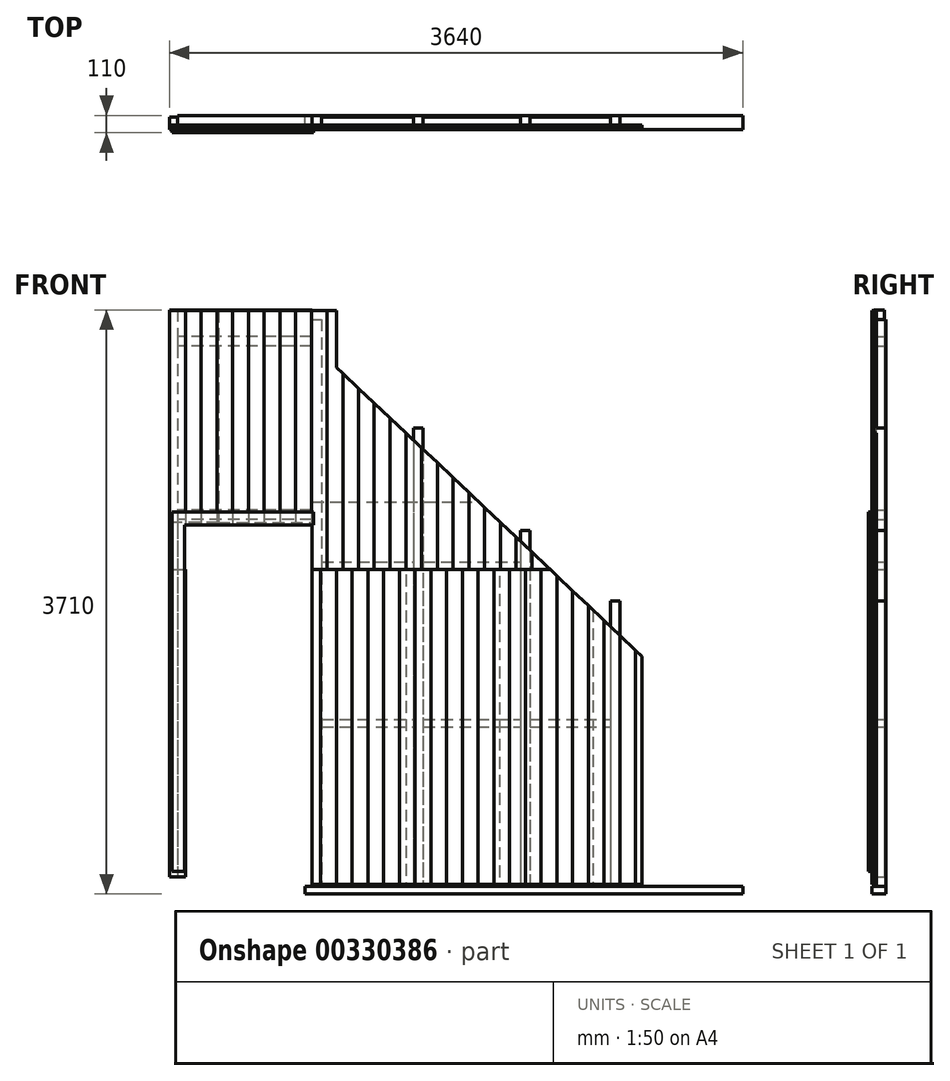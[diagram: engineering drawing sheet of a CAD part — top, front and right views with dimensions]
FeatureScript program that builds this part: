
annotation { "Feature Type Name" : "Feature", "Feature Type Description" : "" }
export const myFeature = defineFeature(function(context is Context, id is Id, definition is map)
    precondition{}
    {
        {
            var Q0;
            Q0=qCreatedBy(makeId("Top.planeOp"),FACE);
            var sketch = newSketch(context, id + "F0", { "sketchPlane" : qUnion([Q0])});
            skLineSegment(sketch, "E0.bottom", {"start": v(0, 0) * mm, "end": v(2780, 0) * mm});
            skLineSegment(sketch, "E0.top", {"start": v(0, 90) * mm, "end": v(2780, 90) * mm});
            skLineSegment(sketch, "E0.left", {"start": v(0, 0) * mm, "end": v(0, 90) * mm});
            skLineSegment(sketch, "E0.right", {"start": v(2780, 0) * mm, "end": v(2780, 90) * mm});
            skSolve(sketch);
        }
        {
            var Q0;
            Q0=makeQuery(id+"F0.imprint","IMPRINT",FACE,{"disambiguationData":[TD([[makeQuery(id+"F0.imprint","IMPRINT",EDGE,{"derivedFrom":sQuery(id+"F0.wireOp",EDGE,"E0.bottom")}),1.0]])]});
            extrude(context, id + "F1", {"entities" : qUnion([Q0]), "depth" : 50 * mm});
        }
        {
            var Q0;
            Q0=qCreatedBy(makeId("Top.planeOp"),FACE);
            var sketch = newSketch(context, id + "F2", { "sketchPlane" : qUnion([Q0])});
            skLineSegment(sketch, "E1", {"start": v(0, 0) * mm, "end": v(10, 0) * mm});
            skLineSegment(sketch, "E2", {"start": v(0, 0) * mm, "end": v(-810, 0) * mm});
            skLineSegment(sketch, "E3.bottom", {"start": v(10, 0) * mm, "end": v(70, 0) * mm});
            skLineSegment(sketch, "E3.top", {"start": v(10, 60) * mm, "end": v(70, 60) * mm});
            skLineSegment(sketch, "E3.left", {"start": v(10, 0) * mm, "end": v(10, 60) * mm});
            skLineSegment(sketch, "E3.right", {"start": v(70, 0) * mm, "end": v(70, 60) * mm});
            skLineSegment(sketch, "E4.bottom", {"start": v(-810, 0) * mm, "end": v(-860, 0) * mm});
            skLineSegment(sketch, "E4.top", {"start": v(-810, 50) * mm, "end": v(-860, 50) * mm});
            skLineSegment(sketch, "E4.left", {"start": v(-810, 0) * mm, "end": v(-810, 50) * mm});
            skLineSegment(sketch, "E4.right", {"start": v(-860, 0) * mm, "end": v(-860, 50) * mm});
            skLineSegment(sketch, "E5", {"start": v(0, 0) * mm, "end": v(2020, 0) * mm});
            skLineSegment(sketch, "E6", {"start": v(70, 60) * mm, "end": v(690, 60) * mm});
            skLineSegment(sketch, "E7.bottom", {"start": v(690, 60) * mm, "end": v(750, 60) * mm});
            skLineSegment(sketch, "E7.top", {"start": v(690, 0) * mm, "end": v(750, 0) * mm});
            skLineSegment(sketch, "E7.left", {"start": v(690, 60) * mm, "end": v(690, 0) * mm});
            skLineSegment(sketch, "E7.right", {"start": v(750, 60) * mm, "end": v(750, 0) * mm});
            skLineSegment(sketch, "E8", {"start": v(750, 60) * mm, "end": v(1370, 60) * mm});
            skLineSegment(sketch, "E9.bottom", {"start": v(1370, 60) * mm, "end": v(1430, 60) * mm});
            skLineSegment(sketch, "E9.top", {"start": v(1370, 0) * mm, "end": v(1430, 0) * mm});
            skLineSegment(sketch, "E9.left", {"start": v(1370, 60) * mm, "end": v(1370, 0) * mm});
            skLineSegment(sketch, "E9.right", {"start": v(1430, 60) * mm, "end": v(1430, 0) * mm});
            skLineSegment(sketch, "E10", {"start": v(1430, 60) * mm, "end": v(1940, 60) * mm});
            skLineSegment(sketch, "E11.bottom", {"start": v(1940, 60) * mm, "end": v(2000, 60) * mm});
            skLineSegment(sketch, "E11.top", {"start": v(1940, 0) * mm, "end": v(2000, 0) * mm});
            skLineSegment(sketch, "E11.left", {"start": v(1940, 60) * mm, "end": v(1940, 0) * mm});
            skLineSegment(sketch, "E11.right", {"start": v(2000, 60) * mm, "end": v(2000, 0) * mm});
            skSolve(sketch);
        }
        {
            var Q0;
            Q0=makeQuery(id+"F2.imprint","IMPRINT",FACE,{"disambiguationData":[TD([[makeQuery(id+"F2.imprint","IMPRINT",EDGE,{"derivedFrom":sQuery(id+"F2.wireOp",EDGE,"E4.bottom")}),-1.0]])]});
            var Q1;
            Q1=makeQuery(id+"F2.imprint","IMPRINT",FACE,{"disambiguationData":[TD([[makeQuery(id+"F2.imprint","IMPRINT",EDGE,{"derivedFrom":sQuery(id+"F2.wireOp",EDGE,"E3.top")}),-1.0]])]});
            extrude(context, id + "F3", {"entities" : qUnion([Q0, Q1]), "depth" : 3600 * mm});
        }
        {
            var Q0;
            Q0=makeQuery(id+"F2.imprint","IMPRINT",FACE,{"disambiguationData":[TD([[makeQuery(id+"F2.imprint","IMPRINT",EDGE,{"derivedFrom":sQuery(id+"F2.wireOp",EDGE,"E7.bottom")}),-1.0]])]});
            extrude(context, id + "F4", {"entities" : qUnion([Q0]), "depth" : 2910 * mm});
        }
        {
            var Q0;
            Q0=makeQuery(id+"F2.imprint","IMPRINT",FACE,{"disambiguationData":[TD([[makeQuery(id+"F2.imprint","IMPRINT",EDGE,{"derivedFrom":sQuery(id+"F2.wireOp",EDGE,"E9.bottom")}),-1.0]])]});
            extrude(context, id + "F5", {"entities" : qUnion([Q0]), "depth" : 2260 * mm});
        }
        {
            var Q0;
            Q0=makeQuery(id+"F2.imprint","IMPRINT",FACE,{"disambiguationData":[TD([[makeQuery(id+"F2.imprint","IMPRINT",EDGE,{"derivedFrom":sQuery(id+"F2.wireOp",EDGE,"E11.bottom")}),-1.0]])]});
            extrude(context, id + "F6", {"entities" : qUnion([Q0]), "depth" : 1810 * mm});
        }
        {
            var Q0;
            Q0=makeQuery(id+"F3.opExtrude","SWEPT_BODY",BODY,{"disambiguationData":[OSD([sQuery(id+"F2.wireOp",EDGE,"E3.top"),sQuery(id+"F2.wireOp",EDGE,"E3.left"),sQuery(id+"F2.wireOp",EDGE,"E3.right"),sQuery(id+"F2.wireOp",EDGE,"E5")])]});
            var Q1;
            Q1=makeQuery(id+"F4.opExtrude","SWEPT_BODY",BODY,{"disambiguationData":[OSD([sQuery(id+"F2.wireOp",EDGE,"E7.bottom"),sQuery(id+"F2.wireOp",EDGE,"E7.top"),sQuery(id+"F2.wireOp",EDGE,"E7.left"),sQuery(id+"F2.wireOp",EDGE,"E7.right")])]});
            var Q2;
            Q2=makeQuery(id+"F3.opExtrude","SWEPT_BODY",BODY,{"disambiguationData":[OSD([sQuery(id+"F2.wireOp",EDGE,"E4.bottom"),sQuery(id+"F2.wireOp",EDGE,"E4.top"),sQuery(id+"F2.wireOp",EDGE,"E4.left"),sQuery(id+"F2.wireOp",EDGE,"E4.right")])]});
            var Q3;
            Q3=makeQuery(id+"F5.opExtrude","SWEPT_BODY",BODY,{"disambiguationData":[OSD([sQuery(id+"F2.wireOp",EDGE,"E9.bottom"),sQuery(id+"F2.wireOp",EDGE,"E9.top"),sQuery(id+"F2.wireOp",EDGE,"E9.left"),sQuery(id+"F2.wireOp",EDGE,"E9.right")])]});
            var Q4;
            Q4=makeQuery(id+"F6.opExtrude","SWEPT_BODY",BODY,{"disambiguationData":[OSD([sQuery(id+"F2.wireOp",EDGE,"E11.bottom"),sQuery(id+"F2.wireOp",EDGE,"E11.top"),sQuery(id+"F2.wireOp",EDGE,"E11.left"),sQuery(id+"F2.wireOp",EDGE,"E11.right")])]});
            transform(context, id + "F7", {"entities" : qUnion([Q0, Q1, Q2, Q3, Q4]), "transformType" : TransformType.TRANSLATION_3D, "dx" : 0 * mm, "dy" : 30 * mm, "dz" : 50 * mm, "makeCopy" : false});
        }
        {
            var Q0;
            Q0=makeQuery(id+"F3.opExtrude","SWEPT_BODY",BODY,{"disambiguationData":[OSD([sQuery(id+"F2.wireOp",EDGE,"E3.top"),sQuery(id+"F2.wireOp",EDGE,"E3.left"),sQuery(id+"F2.wireOp",EDGE,"E3.right"),sQuery(id+"F2.wireOp",EDGE,"E5")])]});
            transform(context, id + "F8", {"entities" : qUnion([Q0]), "transformType" : TransformType.TRANSLATION_3D, "dx" : 35 * mm, "dy" : 0 * mm, "dz" : 0 * mm, "makeCopy" : false});
        }
        {
            var Q0;
            Q0=qCreatedBy(makeId("Top.planeOp"),FACE);
            var sketch = newSketch(context, id + "F9", { "sketchPlane" : qUnion([Q0])});
            skLineSegment(sketch, "E12.bottom", {"start": v(0, 0) * mm, "end": v(595, 0) * mm});
            skLineSegment(sketch, "E12.top", {"start": v(0, -18) * mm, "end": v(595, -18) * mm});
            skLineSegment(sketch, "E12.left", {"start": v(0, 0) * mm, "end": v(0, -18) * mm});
            skLineSegment(sketch, "E12.right", {"start": v(595, 0) * mm, "end": v(595, -18) * mm});
            skSolve(sketch);
        }
        {
            var Q0;
            Q0 = qSketchRegion(id + "F9", true);
            extrude(context, id + "F10", {"entities" : qUnion([Q0]), "depth" : 2440 * mm});
        }
        {
            var Q0;
            Q0=makeQuery(id+"F10.opExtrude","SWEPT_BODY",BODY,{"disambiguationData":[OSD([sQuery(id+"F9.wireOp",EDGE,"E12.bottom"),sQuery(id+"F9.wireOp",EDGE,"E12.top"),sQuery(id+"F9.wireOp",EDGE,"E12.left"),sQuery(id+"F9.wireOp",EDGE,"E12.right")])]});
            transform(context, id + "F11", {"entities" : qUnion([Q0]), "transformType" : TransformType.TRANSLATION_3D, "dx" : 45 * mm, "dy" : 30 * mm, "dz" : -10 * mm, "makeCopy" : false});
        }
        {
            var Q0;
            Q0=makeQuery(id+"F10.opExtrude","SWEPT_BODY",BODY,{"disambiguationData":[OSD([sQuery(id+"F9.wireOp",EDGE,"E12.bottom"),sQuery(id+"F9.wireOp",EDGE,"E12.top"),sQuery(id+"F9.wireOp",EDGE,"E12.left"),sQuery(id+"F9.wireOp",EDGE,"E12.right")])]});
            transform(context, id + "F12", {"entities" : qUnion([Q0]), "transformType" : TransformType.TRANSLATION_3D, "dx" : 595 * mm, "dy" : 0 * mm, "dz" : 0 * mm, "makeCopy" : true});
        }
        {
            var Q0;
            Q0=makeQuery(id+"F12.opPattern","COPY",BODY,{"derivedFrom":makeQuery(id+"F10.opExtrude","SWEPT_BODY",BODY,{"disambiguationData":[OSD([sQuery(id+"F9.wireOp",EDGE,"E12.bottom"),sQuery(id+"F9.wireOp",EDGE,"E12.top"),sQuery(id+"F9.wireOp",EDGE,"E12.left"),sQuery(id+"F9.wireOp",EDGE,"E12.right")])]}),"instanceName":"1"});
            transform(context, id + "F13", {"entities" : qUnion([Q0]), "transformType" : TransformType.TRANSLATION_3D, "dx" : 595 * mm, "dy" : 0 * mm, "dz" : 0 * mm, "makeCopy" : true});
        }
        {
            var Q0;
            Q0=makeQuery(id+"F13.opPattern","COPY",BODY,{"derivedFrom":makeQuery(id+"F12.opPattern","COPY",BODY,{"derivedFrom":makeQuery(id+"F10.opExtrude","SWEPT_BODY",BODY,{"disambiguationData":[OSD([sQuery(id+"F9.wireOp",EDGE,"E12.bottom"),sQuery(id+"F9.wireOp",EDGE,"E12.top"),sQuery(id+"F9.wireOp",EDGE,"E12.left"),sQuery(id+"F9.wireOp",EDGE,"E12.right")])]}),"instanceName":"1"}),"instanceName":"1"});
            transform(context, id + "F14", {"entities" : qUnion([Q0]), "transformType" : TransformType.TRANSLATION_3D, "dx" : 595 * mm, "dy" : 0 * mm, "dz" : 0 * mm, "makeCopy" : true});
        }
        {
            var Q0;
            Q0=makeQuery(id+"F13.opPattern","COPY",BODY,{"derivedFrom":makeQuery(id+"F12.opPattern","COPY",BODY,{"derivedFrom":makeQuery(id+"F10.opExtrude","SWEPT_BODY",BODY,{"disambiguationData":[OSD([sQuery(id+"F9.wireOp",EDGE,"E12.bottom"),sQuery(id+"F9.wireOp",EDGE,"E12.top"),sQuery(id+"F9.wireOp",EDGE,"E12.left"),sQuery(id+"F9.wireOp",EDGE,"E12.right")])]}),"instanceName":"1"}),"instanceName":"1"});
            transform(context, id + "F15", {"entities" : qUnion([Q0]), "transformType" : TransformType.TRANSLATION_3D, "dx" : 0 * mm, "dy" : 0 * mm, "dz" : 2440 * mm, "makeCopy" : true});
        }
        {
            var Q0;
            Q0=makeQuery(id+"F12.opPattern","COPY",BODY,{"derivedFrom":makeQuery(id+"F10.opExtrude","SWEPT_BODY",BODY,{"disambiguationData":[OSD([sQuery(id+"F9.wireOp",EDGE,"E12.bottom"),sQuery(id+"F9.wireOp",EDGE,"E12.top"),sQuery(id+"F9.wireOp",EDGE,"E12.left"),sQuery(id+"F9.wireOp",EDGE,"E12.right")])]}),"instanceName":"1"});
            transform(context, id + "F16", {"entities" : qUnion([Q0]), "transformType" : TransformType.TRANSLATION_3D, "dx" : 0 * mm, "dy" : 0 * mm, "dz" : 2440 * mm, "makeCopy" : true});
        }
        {
            var Q0;
            Q0=makeQuery(id+"F10.opExtrude","SWEPT_BODY",BODY,{"disambiguationData":[OSD([sQuery(id+"F9.wireOp",EDGE,"E12.bottom"),sQuery(id+"F9.wireOp",EDGE,"E12.top"),sQuery(id+"F9.wireOp",EDGE,"E12.left"),sQuery(id+"F9.wireOp",EDGE,"E12.right")])]});
            transform(context, id + "F17", {"entities" : qUnion([Q0]), "transformType" : TransformType.TRANSLATION_3D, "dx" : 0 * mm, "dy" : 0 * mm, "dz" : 2440 * mm, "makeCopy" : true});
        }
        {
            var Q0;
            Q0=makeQuery(id+"F17.opPattern","COPY",BODY,{"derivedFrom":makeQuery(id+"F10.opExtrude","SWEPT_BODY",BODY,{"disambiguationData":[OSD([sQuery(id+"F9.wireOp",EDGE,"E12.bottom"),sQuery(id+"F9.wireOp",EDGE,"E12.top"),sQuery(id+"F9.wireOp",EDGE,"E12.left"),sQuery(id+"F9.wireOp",EDGE,"E12.right")])]}),"instanceName":"1"});
            transform(context, id + "F18", {"entities" : qUnion([Q0]), "transformType" : TransformType.TRANSLATION_3D, "dx" : -595 * mm, "dy" : 0 * mm, "dz" : 0 * mm, "makeCopy" : true});
        }
        {
            var Q0;
            Q0=makeQuery(id+"F18.opPattern","COPY",BODY,{"derivedFrom":makeQuery(id+"F17.opPattern","COPY",BODY,{"derivedFrom":makeQuery(id+"F10.opExtrude","SWEPT_BODY",BODY,{"disambiguationData":[OSD([sQuery(id+"F9.wireOp",EDGE,"E12.bottom"),sQuery(id+"F9.wireOp",EDGE,"E12.top"),sQuery(id+"F9.wireOp",EDGE,"E12.left"),sQuery(id+"F9.wireOp",EDGE,"E12.right")])]}),"instanceName":"1"}),"instanceName":"1"});
            transform(context, id + "F19", {"entities" : qUnion([Q0]), "transformType" : TransformType.TRANSLATION_3D, "dx" : -595 * mm, "dy" : 0 * mm, "dz" : 0 * mm, "makeCopy" : true});
        }
        {
            var Q0;
            Q0=qCreatedBy(makeId("Front.planeOp"),FACE);
            var sketch = newSketch(context, id + "F20", { "sketchPlane" : qUnion([Q0])});
            skLineSegment(sketch, "E13", {"start": v(0, 0) * mm, "end": v(-1939.95, 1834.52) * mm});
            skLineSegment(sketch, "E14", {"start": v(-1939.95, 1834.52) * mm, "end": v(-1939.95, 5834.52) * mm});
            skLineSegment(sketch, "E15", {"start": v(-1939.95, 5834.52) * mm, "end": v(0, 4000) * mm});
            skLineSegment(sketch, "E16", {"start": v(0, 4000) * mm, "end": v(0, 0) * mm});
            skLineSegment(sketch, "E17.bottom", {"start": v(0, 4000) * mm, "end": v(3417.21, 4000) * mm});
            skLineSegment(sketch, "E17.top", {"start": v(0, 0) * mm, "end": v(3417.21, 0) * mm});
            skLineSegment(sketch, "E17.right", {"start": v(3417.21, 4000) * mm, "end": v(3417.21, 0) * mm});
            skLineSegment(sketch, "E18.bottom", {"start": v(3417.21, 0) * mm, "end": v(0, 0) * mm});
            skLineSegment(sketch, "E18.top", {"start": v(3417.21, -2848.11) * mm, "end": v(0, -2848.11) * mm});
            skLineSegment(sketch, "E18.left", {"start": v(3417.21, 0) * mm, "end": v(3417.21, -2848.11) * mm});
            skLineSegment(sketch, "E18.right", {"start": v(0, 0) * mm, "end": v(0, -2848.11) * mm});
            skLineSegment(sketch, "E19", {"start": v(-1939.95, 5834.52) * mm, "end": v(-6116.17, 5834.52) * mm});
            skLineSegment(sketch, "E20", {"start": v(-6116.17, 5834.52) * mm, "end": v(-6116.17, 2194.52) * mm});
            skLineSegment(sketch, "E21", {"start": v(-6116.17, 2194.52) * mm, "end": v(-1939.95, 2194.52) * mm});
            skSolve(sketch);
        }
        {
            var Q0;
            Q0 = qSketchRegion(id + "F20", true);
            extrude(context, id + "F21", {"entities" : qUnion([Q0]), "endBound" : BoundingType.SYMMETRIC, "depth" : 200 * mm});
        }
        {
            var Q0;
            Q0=makeQuery(id+"F21.opExtrude","SWEPT_BODY",BODY,{"disambiguationData":[OSD([sQuery(id+"F20.wireOp",EDGE,"E13"),sQuery(id+"F20.wireOp",EDGE,"E14"),sQuery(id+"F20.wireOp",EDGE,"E15"),sQuery(id+"F20.wireOp",EDGE,"E16")])]});
            transform(context, id + "F22", {"entities" : qUnion([Q0]), "transformType" : TransformType.TRANSLATION_3D, "dx" : 2140 * mm, "dy" : 0 * mm, "dz" : 1450 * mm, "makeCopy" : false});
        }
        {
            var Q0;
            Q0=makeQuery(id+"F15.opPattern","COPY",BODY,{"derivedFrom":makeQuery(id+"F13.opPattern","COPY",BODY,{"derivedFrom":makeQuery(id+"F12.opPattern","COPY",BODY,{"derivedFrom":makeQuery(id+"F10.opExtrude","SWEPT_BODY",BODY,{"disambiguationData":[OSD([sQuery(id+"F9.wireOp",EDGE,"E12.bottom"),sQuery(id+"F9.wireOp",EDGE,"E12.top"),sQuery(id+"F9.wireOp",EDGE,"E12.left"),sQuery(id+"F9.wireOp",EDGE,"E12.right")])]}),"instanceName":"1"}),"instanceName":"1"}),"instanceName":"1"});
            deleteBodies(context, id + "F23", {"entities" : qUnion([Q0])});
        }
        {
            var Q0;
            Q0=qCreatedBy(makeId("Front.planeOp"),FACE);
            var sketch = newSketch(context, id + "F24", { "sketchPlane" : qUnion([Q0])});
            skLineSegment(sketch, "E22.bottom", {"start": v(-1309.86, 3316.96) * mm, "end": v(-884.64, 3316.96) * mm});
            skLineSegment(sketch, "E22.top", {"start": v(-1309.86, 2365.8) * mm, "end": v(-884.64, 2365.8) * mm});
            skLineSegment(sketch, "E22.left", {"start": v(-1309.86, 3316.96) * mm, "end": v(-1309.86, 2365.8) * mm});
            skLineSegment(sketch, "E22.right", {"start": v(-884.64, 3316.96) * mm, "end": v(-884.64, 2365.8) * mm});
            skSolve(sketch);
        }
        {
            var Q0;
            Q0 = qSketchRegion(id + "F24", true);
            extrude(context, id + "F25", {"entities" : qUnion([Q0]), "endBound" : BoundingType.SYMMETRIC, "depth" : 50 * mm});
        }
        {
            var Q0;
            Q0=makeQuery(id+"F25.opExtrude","SWEPT_BODY",BODY,{"disambiguationData":[OSD([sQuery(id+"F24.wireOp",EDGE,"E22.bottom"),sQuery(id+"F24.wireOp",EDGE,"E22.top"),sQuery(id+"F24.wireOp",EDGE,"E22.left"),sQuery(id+"F24.wireOp",EDGE,"E22.right")])]});
            transform(context, id + "F26", {"entities" : qUnion([Q0]), "transformType" : TransformType.TRANSLATION_3D, "dx" : 24.64 * mm, "dy" : 0 * mm, "dz" : 0 * mm, "makeCopy" : false});
        }
        {
            var Q0;
            Q0=makeQuery(id+"F25.opExtrude","SWEPT_BODY",BODY,{"disambiguationData":[OSD([sQuery(id+"F24.wireOp",EDGE,"E22.bottom"),sQuery(id+"F24.wireOp",EDGE,"E22.top"),sQuery(id+"F24.wireOp",EDGE,"E22.left"),sQuery(id+"F24.wireOp",EDGE,"E22.right")])]});
            var Q1;
            Q1=makeQuery(id+"F19.opPattern","COPY",BODY,{"derivedFrom":makeQuery(id+"F18.opPattern","COPY",BODY,{"derivedFrom":makeQuery(id+"F17.opPattern","COPY",BODY,{"derivedFrom":makeQuery(id+"F10.opExtrude","SWEPT_BODY",BODY,{"disambiguationData":[OSD([sQuery(id+"F9.wireOp",EDGE,"E12.bottom"),sQuery(id+"F9.wireOp",EDGE,"E12.top"),sQuery(id+"F9.wireOp",EDGE,"E12.left"),sQuery(id+"F9.wireOp",EDGE,"E12.right")])]}),"instanceName":"1"}),"instanceName":"1"}),"instanceName":"1"});
            booleanBodies(context, id + "F27", {"operationType" : BooleanOperationType.SUBTRACTION, "tools" : qUnion([Q0]), "targets" : qUnion([Q1])});
        }
        {
            var Q0;
            Q0=makeQuery(id+"F18.opPattern","COPY",BODY,{"derivedFrom":makeQuery(id+"F17.opPattern","COPY",BODY,{"derivedFrom":makeQuery(id+"F10.opExtrude","SWEPT_BODY",BODY,{"disambiguationData":[OSD([sQuery(id+"F9.wireOp",EDGE,"E12.bottom"),sQuery(id+"F9.wireOp",EDGE,"E12.top"),sQuery(id+"F9.wireOp",EDGE,"E12.left"),sQuery(id+"F9.wireOp",EDGE,"E12.right")])]}),"instanceName":"1"}),"instanceName":"1"});
            var Q1;
            Q1=makeQuery(id+"F19.opPattern","COPY",BODY,{"derivedFrom":makeQuery(id+"F18.opPattern","COPY",BODY,{"derivedFrom":makeQuery(id+"F17.opPattern","COPY",BODY,{"derivedFrom":makeQuery(id+"F10.opExtrude","SWEPT_BODY",BODY,{"disambiguationData":[OSD([sQuery(id+"F9.wireOp",EDGE,"E12.bottom"),sQuery(id+"F9.wireOp",EDGE,"E12.top"),sQuery(id+"F9.wireOp",EDGE,"E12.left"),sQuery(id+"F9.wireOp",EDGE,"E12.right")])]}),"instanceName":"1"}),"instanceName":"1"}),"instanceName":"1"});
            deleteBodies(context, id + "F28", {"entities" : qUnion([Q0, Q1])});
        }
        {
            var Q0;
            Q0 = qSketchRegion(id + "F9", true);
            extrude(context, id + "F29", {"entities" : qUnion([Q0]), "depth" : 1350 * mm});
        }
        {
            var Q0;
            Q0=qCreatedBy(makeId("Top.planeOp"),FACE);
            var sketch = newSketch(context, id + "F30", { "sketchPlane" : qUnion([Q0])});
            skLineSegment(sketch, "E23.bottom", {"start": v(0, 0) * mm, "end": v(-310, 0) * mm});
            skLineSegment(sketch, "E23.top", {"start": v(0, -18) * mm, "end": v(-310, -18) * mm});
            skLineSegment(sketch, "E23.left", {"start": v(0, 0) * mm, "end": v(0, -18) * mm});
            skLineSegment(sketch, "E23.right", {"start": v(-310, 0) * mm, "end": v(-310, -18) * mm});
            skSolve(sketch);
        }
        {
            var Q0;
            Q0 = qSketchRegion(id + "F30", true);
            extrude(context, id + "F31", {"entities" : qUnion([Q0]), "depth" : 1350 * mm});
        }
        {
            var Q0;
            Q0=makeQuery(id+"F29.opExtrude","SWEPT_BODY",BODY,{"disambiguationData":[OSD([sQuery(id+"F9.wireOp",EDGE,"E12.bottom"),sQuery(id+"F9.wireOp",EDGE,"E12.top"),sQuery(id+"F9.wireOp",EDGE,"E12.left"),sQuery(id+"F9.wireOp",EDGE,"E12.right")])]});
            var Q1;
            Q1=makeQuery(id+"F31.opExtrude","SWEPT_BODY",BODY,{"disambiguationData":[OSD([sQuery(id+"F30.wireOp",EDGE,"E23.bottom"),sQuery(id+"F30.wireOp",EDGE,"E23.top"),sQuery(id+"F30.wireOp",EDGE,"E23.left"),sQuery(id+"F30.wireOp",EDGE,"E23.right")])]});
            transform(context, id + "F32", {"entities" : qUnion([Q0, Q1]), "transformType" : TransformType.TRANSLATION_3D, "dx" : -550 * mm, "dy" : 30 * mm, "dz" : 2300 * mm, "makeCopy" : false});
        }
        {
            var Q0;
            Q0=qCreatedBy(makeId("Top.planeOp"),FACE);
            var sketch = newSketch(context, id + "F33", { "sketchPlane" : qUnion([Q0])});
            skLineSegment(sketch, "E24.bottom", {"start": v(0, 0) * mm, "end": v(-50, 0) * mm});
            skLineSegment(sketch, "E24.top", {"start": v(0, -18) * mm, "end": v(-50, -18) * mm});
            skLineSegment(sketch, "E24.left", {"start": v(0, 0) * mm, "end": v(0, -18) * mm});
            skLineSegment(sketch, "E24.right", {"start": v(-50, 0) * mm, "end": v(-50, -18) * mm});
            skSolve(sketch);
        }
        {
            var Q0;
            Q0 = qSketchRegion(id + "F33", true);
            extrude(context, id + "F34", {"entities" : qUnion([Q0]), "depth" : 2250 * mm});
        }
        {
            var Q0;
            Q0=makeQuery(id+"F34.opExtrude","SWEPT_BODY",BODY,{"disambiguationData":[OSD([sQuery(id+"F33.wireOp",EDGE,"E24.bottom"),sQuery(id+"F33.wireOp",EDGE,"E24.top"),sQuery(id+"F33.wireOp",EDGE,"E24.left"),sQuery(id+"F33.wireOp",EDGE,"E24.right")])]});
            transform(context, id + "F35", {"entities" : qUnion([Q0]), "transformType" : TransformType.TRANSLATION_3D, "dx" : -810 * mm, "dy" : 30 * mm, "dz" : 50 * mm, "makeCopy" : false});
        }
        {
            var Q0;
            Q0=qCreatedBy(makeId("Front.planeOp"),FACE);
            var sketch = newSketch(context, id + "F36", { "sketchPlane" : qUnion([Q0])});
            skLineSegment(sketch, "E25.bottom", {"start": v(0, 0) * mm, "end": v(-80, 0) * mm});
            skLineSegment(sketch, "E25.top", {"start": v(0, 2200) * mm, "end": v(-80, 2200) * mm});
            skLineSegment(sketch, "E25.left", {"start": v(0, 0) * mm, "end": v(0, 2200) * mm});
            skLineSegment(sketch, "E25.right", {"start": v(-80, 0) * mm, "end": v(-80, 2200) * mm});
            skLineSegment(sketch, "E26.bottom", {"start": v(-80, 2200) * mm, "end": v(820, 2200) * mm});
            skLineSegment(sketch, "E26.top", {"start": v(-80, 2280) * mm, "end": v(820, 2280) * mm});
            skLineSegment(sketch, "E26.left", {"start": v(-80, 2200) * mm, "end": v(-80, 2280) * mm});
            skLineSegment(sketch, "E26.right", {"start": v(820, 2200) * mm, "end": v(820, 2280) * mm});
            skSolve(sketch);
        }
        {
            var Q0;
            Q0 = qSketchRegion(id + "F36", true);
            extrude(context, id + "F37", {"entities" : qUnion([Q0]), "depth" : 20 * mm});
        }
        {
            var Q0;
            Q0=makeQuery(id+"F37.opExtrude","SWEPT_BODY",BODY,{"disambiguationData":[OSD([sQuery(id+"F36.wireOp",EDGE,"E25.bottom"),sQuery(id+"F36.wireOp",EDGE,"E25.left"),sQuery(id+"F36.wireOp",EDGE,"E25.right"),sQuery(id+"F36.wireOp",EDGE,"E26.bottom"),sQuery(id+"F36.wireOp",EDGE,"E26.top"),sQuery(id+"F36.wireOp",EDGE,"E26.left"),sQuery(id+"F36.wireOp",EDGE,"E26.right")])]});
            transform(context, id + "F38", {"entities" : qUnion([Q0]), "transformType" : TransformType.TRANSLATION_3D, "dx" : -764.7 * mm, "dy" : 0 * mm, "dz" : 85 * mm, "makeCopy" : false});
        }
        {
            var Q0;
            Q0=makeQuery(id+"F1.opExtrude","SWEPT_BODY",BODY,{"disambiguationData":[OSD([sQuery(id+"F0.wireOp",EDGE,"E0.bottom"),sQuery(id+"F0.wireOp",EDGE,"E0.top"),sQuery(id+"F0.wireOp",EDGE,"E0.left"),sQuery(id+"F0.wireOp",EDGE,"E0.right")])]});
            var Q1;
            Q1=makeQuery(id+"F4.opExtrude","SWEPT_BODY",BODY,{"disambiguationData":[OSD([sQuery(id+"F2.wireOp",EDGE,"E7.bottom"),sQuery(id+"F2.wireOp",EDGE,"E7.top"),sQuery(id+"F2.wireOp",EDGE,"E7.left"),sQuery(id+"F2.wireOp",EDGE,"E7.right")])]});
            var Q2;
            Q2=makeQuery(id+"F5.opExtrude","SWEPT_BODY",BODY,{"disambiguationData":[OSD([sQuery(id+"F2.wireOp",EDGE,"E9.bottom"),sQuery(id+"F2.wireOp",EDGE,"E9.top"),sQuery(id+"F2.wireOp",EDGE,"E9.left"),sQuery(id+"F2.wireOp",EDGE,"E9.right")])]});
            var Q3;
            Q3=makeQuery(id+"F6.opExtrude","SWEPT_BODY",BODY,{"disambiguationData":[OSD([sQuery(id+"F2.wireOp",EDGE,"E11.bottom"),sQuery(id+"F2.wireOp",EDGE,"E11.top"),sQuery(id+"F2.wireOp",EDGE,"E11.left"),sQuery(id+"F2.wireOp",EDGE,"E11.right")])]});
            var Q4;
            Q4=makeQuery(id+"F3.opExtrude","SWEPT_BODY",BODY,{"disambiguationData":[OSD([sQuery(id+"F2.wireOp",EDGE,"E3.top"),sQuery(id+"F2.wireOp",EDGE,"E3.left"),sQuery(id+"F2.wireOp",EDGE,"E3.right"),sQuery(id+"F2.wireOp",EDGE,"E5")])]});
            transform(context, id + "F39", {"entities" : qUnion([Q0, Q1, Q2, Q3, Q4]), "transformType" : TransformType.TRANSLATION_3D, "dx" : 0 * mm, "dy" : 0 * mm, "dz" : -60 * mm, "makeCopy" : false});
        }
        {
            var Q0;
            Q0=qCreatedBy(makeId("Top.planeOp"),FACE);
            var sketch = newSketch(context, id + "F40", { "sketchPlane" : qUnion([Q0])});
            skLineSegment(sketch, "E27.bottom", {"start": v(0, 0) * mm, "end": v(-855, 0) * mm});
            skLineSegment(sketch, "E27.top", {"start": v(0, 60) * mm, "end": v(-855, 60) * mm});
            skLineSegment(sketch, "E27.left", {"start": v(0, 0) * mm, "end": v(0, 60) * mm});
            skLineSegment(sketch, "E27.right", {"start": v(-855, 0) * mm, "end": v(-855, 60) * mm});
            skSolve(sketch);
        }
        {
            var Q0;
            Q0 = qSketchRegion(id + "F40", true);
            extrude(context, id + "F41", {"entities" : qUnion([Q0]), "depth" : 60 * mm});
        }
        {
            var Q0;
            Q0=makeQuery(id+"F41.opExtrude","SWEPT_BODY",BODY,{"disambiguationData":[OSD([sQuery(id+"F40.wireOp",EDGE,"E27.bottom"),sQuery(id+"F40.wireOp",EDGE,"E27.top"),sQuery(id+"F40.wireOp",EDGE,"E27.left"),sQuery(id+"F40.wireOp",EDGE,"E27.right")])]});
            transform(context, id + "F42", {"entities" : qUnion([Q0]), "transformType" : TransformType.TRANSLATION_3D, "dx" : 45 * mm, "dy" : 30 * mm, "dz" : 2320 * mm, "makeCopy" : false});
        }
        {
            var Q0;
            Q0=makeQuery(id+"F41.opExtrude","SWEPT_BODY",BODY,{"disambiguationData":[OSD([sQuery(id+"F40.wireOp",EDGE,"E27.bottom"),sQuery(id+"F40.wireOp",EDGE,"E27.top"),sQuery(id+"F40.wireOp",EDGE,"E27.left"),sQuery(id+"F40.wireOp",EDGE,"E27.right")])]});
            transform(context, id + "F43", {"entities" : qUnion([Q0]), "transformType" : TransformType.TRANSLATION_3D, "dx" : 0 * mm, "dy" : 0 * mm, "dz" : 1100 * mm, "makeCopy" : true});
        }
        {
            var Q0;
            Q0=qCreatedBy(makeId("Top.planeOp"),FACE);
            var sketch = newSketch(context, id + "F44", { "sketchPlane" : qUnion([Q0])});
            skLineSegment(sketch, "E28.bottom", {"start": v(0, 0) * mm, "end": v(585, 0) * mm});
            skLineSegment(sketch, "E28.top", {"start": v(0, 50) * mm, "end": v(585, 50) * mm});
            skLineSegment(sketch, "E28.left", {"start": v(0, 0) * mm, "end": v(0, 50) * mm});
            skLineSegment(sketch, "E28.right", {"start": v(585, 0) * mm, "end": v(585, 50) * mm});
            skSolve(sketch);
        }
        {
            var Q0;
            Q0 = qSketchRegion(id + "F44", true);
            extrude(context, id + "F45", {"entities" : qUnion([Q0]), "depth" : 50 * mm});
        }
        {
            var Q0;
            Q0=makeQuery(id+"F45.opExtrude","SWEPT_BODY",BODY,{"disambiguationData":[OSD([sQuery(id+"F44.wireOp",EDGE,"E28.bottom"),sQuery(id+"F44.wireOp",EDGE,"E28.top"),sQuery(id+"F44.wireOp",EDGE,"E28.left"),sQuery(id+"F44.wireOp",EDGE,"E28.right")])]});
            transform(context, id + "F46", {"entities" : qUnion([Q0]), "transformType" : TransformType.TRANSLATION_3D, "dx" : 105 * mm, "dy" : 30 * mm, "dz" : 1000 * mm, "makeCopy" : false});
        }
        {
            var Q0;
            Q0=makeQuery(id+"F45.opExtrude","SWEPT_BODY",BODY,{"disambiguationData":[OSD([sQuery(id+"F44.wireOp",EDGE,"E28.bottom"),sQuery(id+"F44.wireOp",EDGE,"E28.top"),sQuery(id+"F44.wireOp",EDGE,"E28.left"),sQuery(id+"F44.wireOp",EDGE,"E28.right")])]});
            transform(context, id + "F47", {"entities" : qUnion([Q0]), "transformType" : TransformType.TRANSLATION_3D, "dx" : 0 * mm, "dy" : 0 * mm, "dz" : 1000 * mm, "makeCopy" : true});
        }
        {
            var Q0;
            Q0=qCreatedBy(makeId("Top.planeOp"),FACE);
            var sketch = newSketch(context, id + "F48", { "sketchPlane" : qUnion([Q0])});
            skLineSegment(sketch, "E29.bottom", {"start": v(0, 0) * mm, "end": v(620, 0) * mm});
            skLineSegment(sketch, "E29.top", {"start": v(0, 50) * mm, "end": v(620, 50) * mm});
            skLineSegment(sketch, "E29.left", {"start": v(0, 0) * mm, "end": v(0, 50) * mm});
            skLineSegment(sketch, "E29.right", {"start": v(620, 0) * mm, "end": v(620, 50) * mm});
            skSolve(sketch);
        }
        {
            var Q0;
            Q0 = qSketchRegion(id + "F48", true);
            extrude(context, id + "F49", {"entities" : qUnion([Q0]), "depth" : 50 * mm});
        }
        {
            var Q0;
            Q0=makeQuery(id+"F49.opExtrude","SWEPT_BODY",BODY,{"disambiguationData":[OSD([sQuery(id+"F48.wireOp",EDGE,"E29.bottom"),sQuery(id+"F48.wireOp",EDGE,"E29.top"),sQuery(id+"F48.wireOp",EDGE,"E29.left"),sQuery(id+"F48.wireOp",EDGE,"E29.right")])]});
            transform(context, id + "F50", {"entities" : qUnion([Q0]), "transformType" : TransformType.TRANSLATION_3D, "dx" : 750 * mm, "dy" : 30 * mm, "dz" : 1000 * mm, "makeCopy" : false});
        }
        {
            var Q0;
            Q0=makeQuery(id+"F49.opExtrude","SWEPT_BODY",BODY,{"disambiguationData":[OSD([sQuery(id+"F48.wireOp",EDGE,"E29.bottom"),sQuery(id+"F48.wireOp",EDGE,"E29.top"),sQuery(id+"F48.wireOp",EDGE,"E29.left"),sQuery(id+"F48.wireOp",EDGE,"E29.right")])]});
            transform(context, id + "F51", {"entities" : qUnion([Q0]), "transformType" : TransformType.TRANSLATION_3D, "dx" : 0 * mm, "dy" : 0 * mm, "dz" : 1000 * mm, "makeCopy" : true});
        }
        {
            var Q0;
            Q0=qCreatedBy(makeId("Top.planeOp"),FACE);
            var sketch = newSketch(context, id + "F52", { "sketchPlane" : qUnion([Q0])});
            skLineSegment(sketch, "E30.bottom", {"start": v(0, 0) * mm, "end": v(510, 0) * mm});
            skLineSegment(sketch, "E30.top", {"start": v(0, 50) * mm, "end": v(510, 50) * mm});
            skLineSegment(sketch, "E30.left", {"start": v(0, 0) * mm, "end": v(0, 50) * mm});
            skLineSegment(sketch, "E30.right", {"start": v(510, 0) * mm, "end": v(510, 50) * mm});
            skSolve(sketch);
        }
        {
            var Q0;
            Q0 = qSketchRegion(id + "F52", true);
            extrude(context, id + "F53", {"entities" : qUnion([Q0]), "depth" : 50 * mm});
        }
        {
            var Q0;
            Q0=makeQuery(id+"F53.opExtrude","SWEPT_BODY",BODY,{"disambiguationData":[OSD([sQuery(id+"F52.wireOp",EDGE,"E30.bottom"),sQuery(id+"F52.wireOp",EDGE,"E30.top"),sQuery(id+"F52.wireOp",EDGE,"E30.left"),sQuery(id+"F52.wireOp",EDGE,"E30.right")])]});
            transform(context, id + "F54", {"entities" : qUnion([Q0]), "transformType" : TransformType.TRANSLATION_3D, "dx" : 1430 * mm, "dy" : 30 * mm, "dz" : 1000 * mm, "makeCopy" : false});
        }
        {
            var Q0;
            Q0=qCreatedBy(makeId("Top.planeOp"),FACE);
            var sketch = newSketch(context, id + "F55", { "sketchPlane" : qUnion([Q0])});
            skLineSegment(sketch, "E31.bottom", {"start": v(0, 0) * mm, "end": v(100, 0) * mm});
            skLineSegment(sketch, "E31.top", {"start": v(0, 10) * mm, "end": v(100, 10) * mm});
            skLineSegment(sketch, "E31.left", {"start": v(0, 0) * mm, "end": v(0, 10) * mm});
            skLineSegment(sketch, "E31.right", {"start": v(100, 0) * mm, "end": v(100, 10) * mm});
            skSolve(sketch);
        }
        {
            var Q0;
            Q0 = qSketchRegion(id + "F55", true);
            extrude(context, id + "F56", {"entities" : qUnion([Q0]), "depth" : 2000 * mm});
        }
        {
            var Q0;
            Q0=makeQuery(id+"F56.opExtrude","SWEPT_BODY",BODY,{"disambiguationData":[OSD([sQuery(id+"F55.wireOp",EDGE,"E31.bottom"),sQuery(id+"F55.wireOp",EDGE,"E31.top"),sQuery(id+"F55.wireOp",EDGE,"E31.left"),sQuery(id+"F55.wireOp",EDGE,"E31.right")])]});
            transform(context, id + "F57", {"entities" : qUnion([Q0]), "transformType" : TransformType.TRANSLATION_3D, "dx" : 0 * mm, "dy" : 2 * mm, "dz" : 0 * mm, "makeCopy" : false});
        }
        {
            var Q0;
            Q0=makeQuery(id+"F56.opExtrude","SWEPT_BODY",BODY,{"disambiguationData":[OSD([sQuery(id+"F55.wireOp",EDGE,"E31.bottom"),sQuery(id+"F55.wireOp",EDGE,"E31.top"),sQuery(id+"F55.wireOp",EDGE,"E31.left"),sQuery(id+"F55.wireOp",EDGE,"E31.right")])]});
            transform(context, id + "F58", {"entities" : qUnion([Q0]), "transformType" : TransformType.TRANSLATION_3D, "dx" : 100 * mm, "dy" : 0 * mm, "dz" : 0 * mm, "makeCopy" : true});
        }
        {
            var Q0;
            Q0=makeQuery(id+"F58.opPattern","COPY",BODY,{"derivedFrom":makeQuery(id+"F56.opExtrude","SWEPT_BODY",BODY,{"disambiguationData":[OSD([sQuery(id+"F55.wireOp",EDGE,"E31.bottom"),sQuery(id+"F55.wireOp",EDGE,"E31.top"),sQuery(id+"F55.wireOp",EDGE,"E31.left"),sQuery(id+"F55.wireOp",EDGE,"E31.right")])]}),"instanceName":"1"});
            transform(context, id + "F59", {"entities" : qUnion([Q0]), "transformType" : TransformType.TRANSLATION_3D, "dx" : 100 * mm, "dy" : 0 * mm, "dz" : 0 * mm, "makeCopy" : true});
        }
        {
            var Q0;
            Q0=makeQuery(id+"F59.opPattern","COPY",BODY,{"derivedFrom":makeQuery(id+"F58.opPattern","COPY",BODY,{"derivedFrom":makeQuery(id+"F56.opExtrude","SWEPT_BODY",BODY,{"disambiguationData":[OSD([sQuery(id+"F55.wireOp",EDGE,"E31.bottom"),sQuery(id+"F55.wireOp",EDGE,"E31.top"),sQuery(id+"F55.wireOp",EDGE,"E31.left"),sQuery(id+"F55.wireOp",EDGE,"E31.right")])]}),"instanceName":"1"}),"instanceName":"1"});
            transform(context, id + "F60", {"entities" : qUnion([Q0]), "transformType" : TransformType.TRANSLATION_3D, "dx" : 100 * mm, "dy" : 0 * mm, "dz" : 0 * mm, "makeCopy" : true});
        }
        {
            var Q0;
            Q0=makeQuery(id+"F60.opPattern","COPY",BODY,{"derivedFrom":makeQuery(id+"F59.opPattern","COPY",BODY,{"derivedFrom":makeQuery(id+"F58.opPattern","COPY",BODY,{"derivedFrom":makeQuery(id+"F56.opExtrude","SWEPT_BODY",BODY,{"disambiguationData":[OSD([sQuery(id+"F55.wireOp",EDGE,"E31.bottom"),sQuery(id+"F55.wireOp",EDGE,"E31.top"),sQuery(id+"F55.wireOp",EDGE,"E31.left"),sQuery(id+"F55.wireOp",EDGE,"E31.right")])]}),"instanceName":"1"}),"instanceName":"1"}),"instanceName":"1"});
            transform(context, id + "F61", {"entities" : qUnion([Q0]), "transformType" : TransformType.TRANSLATION_3D, "dx" : 100 * mm, "dy" : 0 * mm, "dz" : 0 * mm, "makeCopy" : true});
        }
        {
            var Q0;
            Q0=makeQuery(id+"F61.opPattern","COPY",BODY,{"derivedFrom":makeQuery(id+"F60.opPattern","COPY",BODY,{"derivedFrom":makeQuery(id+"F59.opPattern","COPY",BODY,{"derivedFrom":makeQuery(id+"F58.opPattern","COPY",BODY,{"derivedFrom":makeQuery(id+"F56.opExtrude","SWEPT_BODY",BODY,{"disambiguationData":[OSD([sQuery(id+"F55.wireOp",EDGE,"E31.bottom"),sQuery(id+"F55.wireOp",EDGE,"E31.top"),sQuery(id+"F55.wireOp",EDGE,"E31.left"),sQuery(id+"F55.wireOp",EDGE,"E31.right")])]}),"instanceName":"1"}),"instanceName":"1"}),"instanceName":"1"}),"instanceName":"1"});
            transform(context, id + "F62", {"entities" : qUnion([Q0]), "transformType" : TransformType.TRANSLATION_3D, "dx" : 100 * mm, "dy" : 0 * mm, "dz" : 0 * mm, "makeCopy" : true});
        }
        {
            var Q0;
            Q0=makeQuery(id+"F62.opPattern","COPY",BODY,{"derivedFrom":makeQuery(id+"F61.opPattern","COPY",BODY,{"derivedFrom":makeQuery(id+"F60.opPattern","COPY",BODY,{"derivedFrom":makeQuery(id+"F59.opPattern","COPY",BODY,{"derivedFrom":makeQuery(id+"F58.opPattern","COPY",BODY,{"derivedFrom":makeQuery(id+"F56.opExtrude","SWEPT_BODY",BODY,{"disambiguationData":[OSD([sQuery(id+"F55.wireOp",EDGE,"E31.bottom"),sQuery(id+"F55.wireOp",EDGE,"E31.top"),sQuery(id+"F55.wireOp",EDGE,"E31.left"),sQuery(id+"F55.wireOp",EDGE,"E31.right")])]}),"instanceName":"1"}),"instanceName":"1"}),"instanceName":"1"}),"instanceName":"1"}),"instanceName":"1"});
            transform(context, id + "F63", {"entities" : qUnion([Q0]), "transformType" : TransformType.TRANSLATION_3D, "dx" : 100 * mm, "dy" : 0 * mm, "dz" : 0 * mm, "makeCopy" : true});
        }
        {
            var Q0;
            Q0=makeQuery(id+"F63.opPattern","COPY",BODY,{"derivedFrom":makeQuery(id+"F62.opPattern","COPY",BODY,{"derivedFrom":makeQuery(id+"F61.opPattern","COPY",BODY,{"derivedFrom":makeQuery(id+"F60.opPattern","COPY",BODY,{"derivedFrom":makeQuery(id+"F59.opPattern","COPY",BODY,{"derivedFrom":makeQuery(id+"F58.opPattern","COPY",BODY,{"derivedFrom":makeQuery(id+"F56.opExtrude","SWEPT_BODY",BODY,{"disambiguationData":[OSD([sQuery(id+"F55.wireOp",EDGE,"E31.bottom"),sQuery(id+"F55.wireOp",EDGE,"E31.top"),sQuery(id+"F55.wireOp",EDGE,"E31.left"),sQuery(id+"F55.wireOp",EDGE,"E31.right")])]}),"instanceName":"1"}),"instanceName":"1"}),"instanceName":"1"}),"instanceName":"1"}),"instanceName":"1"}),"instanceName":"1"});
            transform(context, id + "F64", {"entities" : qUnion([Q0]), "transformType" : TransformType.TRANSLATION_3D, "dx" : 100 * mm, "dy" : 0 * mm, "dz" : 0 * mm, "makeCopy" : true});
        }
        {
            var Q0;
            Q0=makeQuery(id+"F64.opPattern","COPY",BODY,{"derivedFrom":makeQuery(id+"F63.opPattern","COPY",BODY,{"derivedFrom":makeQuery(id+"F62.opPattern","COPY",BODY,{"derivedFrom":makeQuery(id+"F61.opPattern","COPY",BODY,{"derivedFrom":makeQuery(id+"F60.opPattern","COPY",BODY,{"derivedFrom":makeQuery(id+"F59.opPattern","COPY",BODY,{"derivedFrom":makeQuery(id+"F58.opPattern","COPY",BODY,{"derivedFrom":makeQuery(id+"F56.opExtrude","SWEPT_BODY",BODY,{"disambiguationData":[OSD([sQuery(id+"F55.wireOp",EDGE,"E31.bottom"),sQuery(id+"F55.wireOp",EDGE,"E31.top"),sQuery(id+"F55.wireOp",EDGE,"E31.left"),sQuery(id+"F55.wireOp",EDGE,"E31.right")])]}),"instanceName":"1"}),"instanceName":"1"}),"instanceName":"1"}),"instanceName":"1"}),"instanceName":"1"}),"instanceName":"1"}),"instanceName":"1"});
            transform(context, id + "F65", {"entities" : qUnion([Q0]), "transformType" : TransformType.TRANSLATION_3D, "dx" : 100 * mm, "dy" : 0 * mm, "dz" : 0 * mm, "makeCopy" : true});
        }
        {
            var Q0;
            Q0=makeQuery(id+"F65.opPattern","COPY",BODY,{"derivedFrom":makeQuery(id+"F64.opPattern","COPY",BODY,{"derivedFrom":makeQuery(id+"F63.opPattern","COPY",BODY,{"derivedFrom":makeQuery(id+"F62.opPattern","COPY",BODY,{"derivedFrom":makeQuery(id+"F61.opPattern","COPY",BODY,{"derivedFrom":makeQuery(id+"F60.opPattern","COPY",BODY,{"derivedFrom":makeQuery(id+"F59.opPattern","COPY",BODY,{"derivedFrom":makeQuery(id+"F58.opPattern","COPY",BODY,{"derivedFrom":makeQuery(id+"F56.opExtrude","SWEPT_BODY",BODY,{"disambiguationData":[OSD([sQuery(id+"F55.wireOp",EDGE,"E31.bottom"),sQuery(id+"F55.wireOp",EDGE,"E31.top"),sQuery(id+"F55.wireOp",EDGE,"E31.left"),sQuery(id+"F55.wireOp",EDGE,"E31.right")])]}),"instanceName":"1"}),"instanceName":"1"}),"instanceName":"1"}),"instanceName":"1"}),"instanceName":"1"}),"instanceName":"1"}),"instanceName":"1"}),"instanceName":"1"});
            transform(context, id + "F66", {"entities" : qUnion([Q0]), "transformType" : TransformType.TRANSLATION_3D, "dx" : 100 * mm, "dy" : 0 * mm, "dz" : 0 * mm, "makeCopy" : true});
        }
        {
            var Q0;
            Q0=makeQuery(id+"F66.opPattern","COPY",BODY,{"derivedFrom":makeQuery(id+"F65.opPattern","COPY",BODY,{"derivedFrom":makeQuery(id+"F64.opPattern","COPY",BODY,{"derivedFrom":makeQuery(id+"F63.opPattern","COPY",BODY,{"derivedFrom":makeQuery(id+"F62.opPattern","COPY",BODY,{"derivedFrom":makeQuery(id+"F61.opPattern","COPY",BODY,{"derivedFrom":makeQuery(id+"F60.opPattern","COPY",BODY,{"derivedFrom":makeQuery(id+"F59.opPattern","COPY",BODY,{"derivedFrom":makeQuery(id+"F58.opPattern","COPY",BODY,{"derivedFrom":makeQuery(id+"F56.opExtrude","SWEPT_BODY",BODY,{"disambiguationData":[OSD([sQuery(id+"F55.wireOp",EDGE,"E31.bottom"),sQuery(id+"F55.wireOp",EDGE,"E31.top"),sQuery(id+"F55.wireOp",EDGE,"E31.left"),sQuery(id+"F55.wireOp",EDGE,"E31.right")])]}),"instanceName":"1"}),"instanceName":"1"}),"instanceName":"1"}),"instanceName":"1"}),"instanceName":"1"}),"instanceName":"1"}),"instanceName":"1"}),"instanceName":"1"}),"instanceName":"1"});
            transform(context, id + "F67", {"entities" : qUnion([Q0]), "transformType" : TransformType.TRANSLATION_3D, "dx" : 100 * mm, "dy" : 0 * mm, "dz" : 0 * mm, "makeCopy" : true});
        }
        {
            var Q0;
            Q0=makeQuery(id+"F67.opPattern","COPY",BODY,{"derivedFrom":makeQuery(id+"F66.opPattern","COPY",BODY,{"derivedFrom":makeQuery(id+"F65.opPattern","COPY",BODY,{"derivedFrom":makeQuery(id+"F64.opPattern","COPY",BODY,{"derivedFrom":makeQuery(id+"F63.opPattern","COPY",BODY,{"derivedFrom":makeQuery(id+"F62.opPattern","COPY",BODY,{"derivedFrom":makeQuery(id+"F61.opPattern","COPY",BODY,{"derivedFrom":makeQuery(id+"F60.opPattern","COPY",BODY,{"derivedFrom":makeQuery(id+"F59.opPattern","COPY",BODY,{"derivedFrom":makeQuery(id+"F58.opPattern","COPY",BODY,{"derivedFrom":makeQuery(id+"F56.opExtrude","SWEPT_BODY",BODY,{"disambiguationData":[OSD([sQuery(id+"F55.wireOp",EDGE,"E31.bottom"),sQuery(id+"F55.wireOp",EDGE,"E31.top"),sQuery(id+"F55.wireOp",EDGE,"E31.left"),sQuery(id+"F55.wireOp",EDGE,"E31.right")])]}),"instanceName":"1"}),"instanceName":"1"}),"instanceName":"1"}),"instanceName":"1"}),"instanceName":"1"}),"instanceName":"1"}),"instanceName":"1"}),"instanceName":"1"}),"instanceName":"1"}),"instanceName":"1"});
            transform(context, id + "F68", {"entities" : qUnion([Q0]), "transformType" : TransformType.TRANSLATION_3D, "dx" : 100 * mm, "dy" : 0 * mm, "dz" : 0 * mm, "makeCopy" : true});
        }
        {
            var Q0;
            Q0=makeQuery(id+"F68.opPattern","COPY",BODY,{"derivedFrom":makeQuery(id+"F67.opPattern","COPY",BODY,{"derivedFrom":makeQuery(id+"F66.opPattern","COPY",BODY,{"derivedFrom":makeQuery(id+"F65.opPattern","COPY",BODY,{"derivedFrom":makeQuery(id+"F64.opPattern","COPY",BODY,{"derivedFrom":makeQuery(id+"F63.opPattern","COPY",BODY,{"derivedFrom":makeQuery(id+"F62.opPattern","COPY",BODY,{"derivedFrom":makeQuery(id+"F61.opPattern","COPY",BODY,{"derivedFrom":makeQuery(id+"F60.opPattern","COPY",BODY,{"derivedFrom":makeQuery(id+"F59.opPattern","COPY",BODY,{"derivedFrom":makeQuery(id+"F58.opPattern","COPY",BODY,{"derivedFrom":makeQuery(id+"F56.opExtrude","SWEPT_BODY",BODY,{"disambiguationData":[OSD([sQuery(id+"F55.wireOp",EDGE,"E31.bottom"),sQuery(id+"F55.wireOp",EDGE,"E31.top"),sQuery(id+"F55.wireOp",EDGE,"E31.left"),sQuery(id+"F55.wireOp",EDGE,"E31.right")])]}),"instanceName":"1"}),"instanceName":"1"}),"instanceName":"1"}),"instanceName":"1"}),"instanceName":"1"}),"instanceName":"1"}),"instanceName":"1"}),"instanceName":"1"}),"instanceName":"1"}),"instanceName":"1"}),"instanceName":"1"});
            transform(context, id + "F69", {"entities" : qUnion([Q0]), "transformType" : TransformType.TRANSLATION_3D, "dx" : 100 * mm, "dy" : 0 * mm, "dz" : 0 * mm, "makeCopy" : true});
        }
        {
            var Q0;
            Q0=makeQuery(id+"F69.opPattern","COPY",BODY,{"derivedFrom":makeQuery(id+"F68.opPattern","COPY",BODY,{"derivedFrom":makeQuery(id+"F67.opPattern","COPY",BODY,{"derivedFrom":makeQuery(id+"F66.opPattern","COPY",BODY,{"derivedFrom":makeQuery(id+"F65.opPattern","COPY",BODY,{"derivedFrom":makeQuery(id+"F64.opPattern","COPY",BODY,{"derivedFrom":makeQuery(id+"F63.opPattern","COPY",BODY,{"derivedFrom":makeQuery(id+"F62.opPattern","COPY",BODY,{"derivedFrom":makeQuery(id+"F61.opPattern","COPY",BODY,{"derivedFrom":makeQuery(id+"F60.opPattern","COPY",BODY,{"derivedFrom":makeQuery(id+"F59.opPattern","COPY",BODY,{"derivedFrom":makeQuery(id+"F58.opPattern","COPY",BODY,{"derivedFrom":makeQuery(id+"F56.opExtrude","SWEPT_BODY",BODY,{"disambiguationData":[OSD([sQuery(id+"F55.wireOp",EDGE,"E31.bottom"),sQuery(id+"F55.wireOp",EDGE,"E31.top"),sQuery(id+"F55.wireOp",EDGE,"E31.left"),sQuery(id+"F55.wireOp",EDGE,"E31.right")])]}),"instanceName":"1"}),"instanceName":"1"}),"instanceName":"1"}),"instanceName":"1"}),"instanceName":"1"}),"instanceName":"1"}),"instanceName":"1"}),"instanceName":"1"}),"instanceName":"1"}),"instanceName":"1"}),"instanceName":"1"}),"instanceName":"1"});
            transform(context, id + "F70", {"entities" : qUnion([Q0]), "transformType" : TransformType.TRANSLATION_3D, "dx" : 100 * mm, "dy" : 0 * mm, "dz" : 0 * mm, "makeCopy" : true});
        }
        {
            var Q0;
            Q0=makeQuery(id+"F70.opPattern","COPY",BODY,{"derivedFrom":makeQuery(id+"F69.opPattern","COPY",BODY,{"derivedFrom":makeQuery(id+"F68.opPattern","COPY",BODY,{"derivedFrom":makeQuery(id+"F67.opPattern","COPY",BODY,{"derivedFrom":makeQuery(id+"F66.opPattern","COPY",BODY,{"derivedFrom":makeQuery(id+"F65.opPattern","COPY",BODY,{"derivedFrom":makeQuery(id+"F64.opPattern","COPY",BODY,{"derivedFrom":makeQuery(id+"F63.opPattern","COPY",BODY,{"derivedFrom":makeQuery(id+"F62.opPattern","COPY",BODY,{"derivedFrom":makeQuery(id+"F61.opPattern","COPY",BODY,{"derivedFrom":makeQuery(id+"F60.opPattern","COPY",BODY,{"derivedFrom":makeQuery(id+"F59.opPattern","COPY",BODY,{"derivedFrom":makeQuery(id+"F58.opPattern","COPY",BODY,{"derivedFrom":makeQuery(id+"F56.opExtrude","SWEPT_BODY",BODY,{"disambiguationData":[OSD([sQuery(id+"F55.wireOp",EDGE,"E31.bottom"),sQuery(id+"F55.wireOp",EDGE,"E31.top"),sQuery(id+"F55.wireOp",EDGE,"E31.left"),sQuery(id+"F55.wireOp",EDGE,"E31.right")])]}),"instanceName":"1"}),"instanceName":"1"}),"instanceName":"1"}),"instanceName":"1"}),"instanceName":"1"}),"instanceName":"1"}),"instanceName":"1"}),"instanceName":"1"}),"instanceName":"1"}),"instanceName":"1"}),"instanceName":"1"}),"instanceName":"1"}),"instanceName":"1"});
            transform(context, id + "F71", {"entities" : qUnion([Q0]), "transformType" : TransformType.TRANSLATION_3D, "dx" : 100 * mm, "dy" : 0 * mm, "dz" : 0 * mm, "makeCopy" : true});
        }
        {
            var Q0;
            Q0=makeQuery(id+"F71.opPattern","COPY",BODY,{"derivedFrom":makeQuery(id+"F70.opPattern","COPY",BODY,{"derivedFrom":makeQuery(id+"F69.opPattern","COPY",BODY,{"derivedFrom":makeQuery(id+"F68.opPattern","COPY",BODY,{"derivedFrom":makeQuery(id+"F67.opPattern","COPY",BODY,{"derivedFrom":makeQuery(id+"F66.opPattern","COPY",BODY,{"derivedFrom":makeQuery(id+"F65.opPattern","COPY",BODY,{"derivedFrom":makeQuery(id+"F64.opPattern","COPY",BODY,{"derivedFrom":makeQuery(id+"F63.opPattern","COPY",BODY,{"derivedFrom":makeQuery(id+"F62.opPattern","COPY",BODY,{"derivedFrom":makeQuery(id+"F61.opPattern","COPY",BODY,{"derivedFrom":makeQuery(id+"F60.opPattern","COPY",BODY,{"derivedFrom":makeQuery(id+"F59.opPattern","COPY",BODY,{"derivedFrom":makeQuery(id+"F58.opPattern","COPY",BODY,{"derivedFrom":makeQuery(id+"F56.opExtrude","SWEPT_BODY",BODY,{"disambiguationData":[OSD([sQuery(id+"F55.wireOp",EDGE,"E31.bottom"),sQuery(id+"F55.wireOp",EDGE,"E31.top"),sQuery(id+"F55.wireOp",EDGE,"E31.left"),sQuery(id+"F55.wireOp",EDGE,"E31.right")])]}),"instanceName":"1"}),"instanceName":"1"}),"instanceName":"1"}),"instanceName":"1"}),"instanceName":"1"}),"instanceName":"1"}),"instanceName":"1"}),"instanceName":"1"}),"instanceName":"1"}),"instanceName":"1"}),"instanceName":"1"}),"instanceName":"1"}),"instanceName":"1"}),"instanceName":"1"});
            transform(context, id + "F72", {"entities" : qUnion([Q0]), "transformType" : TransformType.TRANSLATION_3D, "dx" : 100 * mm, "dy" : 0 * mm, "dz" : 0 * mm, "makeCopy" : true});
        }
        {
            var Q0;
            Q0=makeQuery(id+"F72.opPattern","COPY",BODY,{"derivedFrom":makeQuery(id+"F71.opPattern","COPY",BODY,{"derivedFrom":makeQuery(id+"F70.opPattern","COPY",BODY,{"derivedFrom":makeQuery(id+"F69.opPattern","COPY",BODY,{"derivedFrom":makeQuery(id+"F68.opPattern","COPY",BODY,{"derivedFrom":makeQuery(id+"F67.opPattern","COPY",BODY,{"derivedFrom":makeQuery(id+"F66.opPattern","COPY",BODY,{"derivedFrom":makeQuery(id+"F65.opPattern","COPY",BODY,{"derivedFrom":makeQuery(id+"F64.opPattern","COPY",BODY,{"derivedFrom":makeQuery(id+"F63.opPattern","COPY",BODY,{"derivedFrom":makeQuery(id+"F62.opPattern","COPY",BODY,{"derivedFrom":makeQuery(id+"F61.opPattern","COPY",BODY,{"derivedFrom":makeQuery(id+"F60.opPattern","COPY",BODY,{"derivedFrom":makeQuery(id+"F59.opPattern","COPY",BODY,{"derivedFrom":makeQuery(id+"F58.opPattern","COPY",BODY,{"derivedFrom":makeQuery(id+"F56.opExtrude","SWEPT_BODY",BODY,{"disambiguationData":[OSD([sQuery(id+"F55.wireOp",EDGE,"E31.bottom"),sQuery(id+"F55.wireOp",EDGE,"E31.top"),sQuery(id+"F55.wireOp",EDGE,"E31.left"),sQuery(id+"F55.wireOp",EDGE,"E31.right")])]}),"instanceName":"1"}),"instanceName":"1"}),"instanceName":"1"}),"instanceName":"1"}),"instanceName":"1"}),"instanceName":"1"}),"instanceName":"1"}),"instanceName":"1"}),"instanceName":"1"}),"instanceName":"1"}),"instanceName":"1"}),"instanceName":"1"}),"instanceName":"1"}),"instanceName":"1"}),"instanceName":"1"});
            transform(context, id + "F73", {"entities" : qUnion([Q0]), "transformType" : TransformType.TRANSLATION_3D, "dx" : 100 * mm, "dy" : 0 * mm, "dz" : 0 * mm, "makeCopy" : true});
        }
        {
            var Q0;
            Q0=makeQuery(id+"F73.opPattern","COPY",BODY,{"derivedFrom":makeQuery(id+"F72.opPattern","COPY",BODY,{"derivedFrom":makeQuery(id+"F71.opPattern","COPY",BODY,{"derivedFrom":makeQuery(id+"F70.opPattern","COPY",BODY,{"derivedFrom":makeQuery(id+"F69.opPattern","COPY",BODY,{"derivedFrom":makeQuery(id+"F68.opPattern","COPY",BODY,{"derivedFrom":makeQuery(id+"F67.opPattern","COPY",BODY,{"derivedFrom":makeQuery(id+"F66.opPattern","COPY",BODY,{"derivedFrom":makeQuery(id+"F65.opPattern","COPY",BODY,{"derivedFrom":makeQuery(id+"F64.opPattern","COPY",BODY,{"derivedFrom":makeQuery(id+"F63.opPattern","COPY",BODY,{"derivedFrom":makeQuery(id+"F62.opPattern","COPY",BODY,{"derivedFrom":makeQuery(id+"F61.opPattern","COPY",BODY,{"derivedFrom":makeQuery(id+"F60.opPattern","COPY",BODY,{"derivedFrom":makeQuery(id+"F59.opPattern","COPY",BODY,{"derivedFrom":makeQuery(id+"F58.opPattern","COPY",BODY,{"derivedFrom":makeQuery(id+"F56.opExtrude","SWEPT_BODY",BODY,{"disambiguationData":[OSD([sQuery(id+"F55.wireOp",EDGE,"E31.bottom"),sQuery(id+"F55.wireOp",EDGE,"E31.top"),sQuery(id+"F55.wireOp",EDGE,"E31.left"),sQuery(id+"F55.wireOp",EDGE,"E31.right")])]}),"instanceName":"1"}),"instanceName":"1"}),"instanceName":"1"}),"instanceName":"1"}),"instanceName":"1"}),"instanceName":"1"}),"instanceName":"1"}),"instanceName":"1"}),"instanceName":"1"}),"instanceName":"1"}),"instanceName":"1"}),"instanceName":"1"}),"instanceName":"1"}),"instanceName":"1"}),"instanceName":"1"}),"instanceName":"1"});
            transform(context, id + "F74", {"entities" : qUnion([Q0]), "transformType" : TransformType.TRANSLATION_3D, "dx" : 100 * mm, "dy" : 0 * mm, "dz" : 0 * mm, "makeCopy" : true});
        }
        {
            var Q0;
            Q0=makeQuery(id+"F74.opPattern","COPY",BODY,{"derivedFrom":makeQuery(id+"F73.opPattern","COPY",BODY,{"derivedFrom":makeQuery(id+"F72.opPattern","COPY",BODY,{"derivedFrom":makeQuery(id+"F71.opPattern","COPY",BODY,{"derivedFrom":makeQuery(id+"F70.opPattern","COPY",BODY,{"derivedFrom":makeQuery(id+"F69.opPattern","COPY",BODY,{"derivedFrom":makeQuery(id+"F68.opPattern","COPY",BODY,{"derivedFrom":makeQuery(id+"F67.opPattern","COPY",BODY,{"derivedFrom":makeQuery(id+"F66.opPattern","COPY",BODY,{"derivedFrom":makeQuery(id+"F65.opPattern","COPY",BODY,{"derivedFrom":makeQuery(id+"F64.opPattern","COPY",BODY,{"derivedFrom":makeQuery(id+"F63.opPattern","COPY",BODY,{"derivedFrom":makeQuery(id+"F62.opPattern","COPY",BODY,{"derivedFrom":makeQuery(id+"F61.opPattern","COPY",BODY,{"derivedFrom":makeQuery(id+"F60.opPattern","COPY",BODY,{"derivedFrom":makeQuery(id+"F59.opPattern","COPY",BODY,{"derivedFrom":makeQuery(id+"F58.opPattern","COPY",BODY,{"derivedFrom":makeQuery(id+"F56.opExtrude","SWEPT_BODY",BODY,{"disambiguationData":[OSD([sQuery(id+"F55.wireOp",EDGE,"E31.bottom"),sQuery(id+"F55.wireOp",EDGE,"E31.top"),sQuery(id+"F55.wireOp",EDGE,"E31.left"),sQuery(id+"F55.wireOp",EDGE,"E31.right")])]}),"instanceName":"1"}),"instanceName":"1"}),"instanceName":"1"}),"instanceName":"1"}),"instanceName":"1"}),"instanceName":"1"}),"instanceName":"1"}),"instanceName":"1"}),"instanceName":"1"}),"instanceName":"1"}),"instanceName":"1"}),"instanceName":"1"}),"instanceName":"1"}),"instanceName":"1"}),"instanceName":"1"}),"instanceName":"1"}),"instanceName":"1"});
            transform(context, id + "F75", {"entities" : qUnion([Q0]), "transformType" : TransformType.TRANSLATION_3D, "dx" : 100 * mm, "dy" : 0 * mm, "dz" : 0 * mm, "makeCopy" : true});
        }
        {
            var Q0;
            Q0=makeQuery(id+"F75.opPattern","COPY",BODY,{"derivedFrom":makeQuery(id+"F74.opPattern","COPY",BODY,{"derivedFrom":makeQuery(id+"F73.opPattern","COPY",BODY,{"derivedFrom":makeQuery(id+"F72.opPattern","COPY",BODY,{"derivedFrom":makeQuery(id+"F71.opPattern","COPY",BODY,{"derivedFrom":makeQuery(id+"F70.opPattern","COPY",BODY,{"derivedFrom":makeQuery(id+"F69.opPattern","COPY",BODY,{"derivedFrom":makeQuery(id+"F68.opPattern","COPY",BODY,{"derivedFrom":makeQuery(id+"F67.opPattern","COPY",BODY,{"derivedFrom":makeQuery(id+"F66.opPattern","COPY",BODY,{"derivedFrom":makeQuery(id+"F65.opPattern","COPY",BODY,{"derivedFrom":makeQuery(id+"F64.opPattern","COPY",BODY,{"derivedFrom":makeQuery(id+"F63.opPattern","COPY",BODY,{"derivedFrom":makeQuery(id+"F62.opPattern","COPY",BODY,{"derivedFrom":makeQuery(id+"F61.opPattern","COPY",BODY,{"derivedFrom":makeQuery(id+"F60.opPattern","COPY",BODY,{"derivedFrom":makeQuery(id+"F59.opPattern","COPY",BODY,{"derivedFrom":makeQuery(id+"F58.opPattern","COPY",BODY,{"derivedFrom":makeQuery(id+"F56.opExtrude","SWEPT_BODY",BODY,{"disambiguationData":[OSD([sQuery(id+"F55.wireOp",EDGE,"E31.bottom"),sQuery(id+"F55.wireOp",EDGE,"E31.top"),sQuery(id+"F55.wireOp",EDGE,"E31.left"),sQuery(id+"F55.wireOp",EDGE,"E31.right")])]}),"instanceName":"1"}),"instanceName":"1"}),"instanceName":"1"}),"instanceName":"1"}),"instanceName":"1"}),"instanceName":"1"}),"instanceName":"1"}),"instanceName":"1"}),"instanceName":"1"}),"instanceName":"1"}),"instanceName":"1"}),"instanceName":"1"}),"instanceName":"1"}),"instanceName":"1"}),"instanceName":"1"}),"instanceName":"1"}),"instanceName":"1"}),"instanceName":"1"});
            transform(context, id + "F76", {"entities" : qUnion([Q0]), "transformType" : TransformType.TRANSLATION_3D, "dx" : 100 * mm, "dy" : 0 * mm, "dz" : 0 * mm, "makeCopy" : true});
        }
        {
            var Q0;
            Q0=makeQuery(id+"F76.opPattern","COPY",BODY,{"derivedFrom":makeQuery(id+"F75.opPattern","COPY",BODY,{"derivedFrom":makeQuery(id+"F74.opPattern","COPY",BODY,{"derivedFrom":makeQuery(id+"F73.opPattern","COPY",BODY,{"derivedFrom":makeQuery(id+"F72.opPattern","COPY",BODY,{"derivedFrom":makeQuery(id+"F71.opPattern","COPY",BODY,{"derivedFrom":makeQuery(id+"F70.opPattern","COPY",BODY,{"derivedFrom":makeQuery(id+"F69.opPattern","COPY",BODY,{"derivedFrom":makeQuery(id+"F68.opPattern","COPY",BODY,{"derivedFrom":makeQuery(id+"F67.opPattern","COPY",BODY,{"derivedFrom":makeQuery(id+"F66.opPattern","COPY",BODY,{"derivedFrom":makeQuery(id+"F65.opPattern","COPY",BODY,{"derivedFrom":makeQuery(id+"F64.opPattern","COPY",BODY,{"derivedFrom":makeQuery(id+"F63.opPattern","COPY",BODY,{"derivedFrom":makeQuery(id+"F62.opPattern","COPY",BODY,{"derivedFrom":makeQuery(id+"F61.opPattern","COPY",BODY,{"derivedFrom":makeQuery(id+"F60.opPattern","COPY",BODY,{"derivedFrom":makeQuery(id+"F59.opPattern","COPY",BODY,{"derivedFrom":makeQuery(id+"F58.opPattern","COPY",BODY,{"derivedFrom":makeQuery(id+"F56.opExtrude","SWEPT_BODY",BODY,{"disambiguationData":[OSD([sQuery(id+"F55.wireOp",EDGE,"E31.bottom"),sQuery(id+"F55.wireOp",EDGE,"E31.top"),sQuery(id+"F55.wireOp",EDGE,"E31.left"),sQuery(id+"F55.wireOp",EDGE,"E31.right")])]}),"instanceName":"1"}),"instanceName":"1"}),"instanceName":"1"}),"instanceName":"1"}),"instanceName":"1"}),"instanceName":"1"}),"instanceName":"1"}),"instanceName":"1"}),"instanceName":"1"}),"instanceName":"1"}),"instanceName":"1"}),"instanceName":"1"}),"instanceName":"1"}),"instanceName":"1"}),"instanceName":"1"}),"instanceName":"1"}),"instanceName":"1"}),"instanceName":"1"}),"instanceName":"1"});
            transform(context, id + "F77", {"entities" : qUnion([Q0]), "transformType" : TransformType.TRANSLATION_3D, "dx" : 100 * mm, "dy" : 0 * mm, "dz" : 0 * mm, "makeCopy" : true});
        }
        {
            var Q0;
            Q0=makeQuery(id+"F77.opPattern","COPY",BODY,{"derivedFrom":makeQuery(id+"F76.opPattern","COPY",BODY,{"derivedFrom":makeQuery(id+"F75.opPattern","COPY",BODY,{"derivedFrom":makeQuery(id+"F74.opPattern","COPY",BODY,{"derivedFrom":makeQuery(id+"F73.opPattern","COPY",BODY,{"derivedFrom":makeQuery(id+"F72.opPattern","COPY",BODY,{"derivedFrom":makeQuery(id+"F71.opPattern","COPY",BODY,{"derivedFrom":makeQuery(id+"F70.opPattern","COPY",BODY,{"derivedFrom":makeQuery(id+"F69.opPattern","COPY",BODY,{"derivedFrom":makeQuery(id+"F68.opPattern","COPY",BODY,{"derivedFrom":makeQuery(id+"F67.opPattern","COPY",BODY,{"derivedFrom":makeQuery(id+"F66.opPattern","COPY",BODY,{"derivedFrom":makeQuery(id+"F65.opPattern","COPY",BODY,{"derivedFrom":makeQuery(id+"F64.opPattern","COPY",BODY,{"derivedFrom":makeQuery(id+"F63.opPattern","COPY",BODY,{"derivedFrom":makeQuery(id+"F62.opPattern","COPY",BODY,{"derivedFrom":makeQuery(id+"F61.opPattern","COPY",BODY,{"derivedFrom":makeQuery(id+"F60.opPattern","COPY",BODY,{"derivedFrom":makeQuery(id+"F59.opPattern","COPY",BODY,{"derivedFrom":makeQuery(id+"F58.opPattern","COPY",BODY,{"derivedFrom":makeQuery(id+"F56.opExtrude","SWEPT_BODY",BODY,{"disambiguationData":[OSD([sQuery(id+"F55.wireOp",EDGE,"E31.bottom"),sQuery(id+"F55.wireOp",EDGE,"E31.top"),sQuery(id+"F55.wireOp",EDGE,"E31.left"),sQuery(id+"F55.wireOp",EDGE,"E31.right")])]}),"instanceName":"1"}),"instanceName":"1"}),"instanceName":"1"}),"instanceName":"1"}),"instanceName":"1"}),"instanceName":"1"}),"instanceName":"1"}),"instanceName":"1"}),"instanceName":"1"}),"instanceName":"1"}),"instanceName":"1"}),"instanceName":"1"}),"instanceName":"1"}),"instanceName":"1"}),"instanceName":"1"}),"instanceName":"1"}),"instanceName":"1"}),"instanceName":"1"}),"instanceName":"1"}),"instanceName":"1"});
            transform(context, id + "F78", {"entities" : qUnion([Q0]), "transformType" : TransformType.TRANSLATION_3D, "dx" : 100 * mm, "dy" : 0 * mm, "dz" : 0 * mm, "makeCopy" : true});
        }
        {
            var Q0;
            Q0=makeQuery(id+"F56.opExtrude","SWEPT_BODY",BODY,{"disambiguationData":[OSD([sQuery(id+"F55.wireOp",EDGE,"E31.bottom"),sQuery(id+"F55.wireOp",EDGE,"E31.top"),sQuery(id+"F55.wireOp",EDGE,"E31.left"),sQuery(id+"F55.wireOp",EDGE,"E31.right")])]});
            transform(context, id + "F79", {"entities" : qUnion([Q0]), "transformType" : TransformType.TRANSLATION_3D, "dx" : -860 * mm, "dy" : 0 * mm, "dz" : 2000 * mm, "makeCopy" : true});
        }
        {
            var Q0;
            Q0=makeQuery(id+"F79.opPattern","COPY",BODY,{"derivedFrom":makeQuery(id+"F56.opExtrude","SWEPT_BODY",BODY,{"disambiguationData":[OSD([sQuery(id+"F55.wireOp",EDGE,"E31.bottom"),sQuery(id+"F55.wireOp",EDGE,"E31.top"),sQuery(id+"F55.wireOp",EDGE,"E31.left"),sQuery(id+"F55.wireOp",EDGE,"E31.right")])]}),"instanceName":"1"});
            transform(context, id + "F80", {"entities" : qUnion([Q0]), "transformType" : TransformType.TRANSLATION_3D, "dx" : 100 * mm, "dy" : 0 * mm, "dz" : 0 * mm, "makeCopy" : true});
        }
        {
            var Q0;
            Q0=makeQuery(id+"F80.opPattern","COPY",BODY,{"derivedFrom":makeQuery(id+"F79.opPattern","COPY",BODY,{"derivedFrom":makeQuery(id+"F56.opExtrude","SWEPT_BODY",BODY,{"disambiguationData":[OSD([sQuery(id+"F55.wireOp",EDGE,"E31.bottom"),sQuery(id+"F55.wireOp",EDGE,"E31.top"),sQuery(id+"F55.wireOp",EDGE,"E31.left"),sQuery(id+"F55.wireOp",EDGE,"E31.right")])]}),"instanceName":"1"}),"instanceName":"1"});
            transform(context, id + "F81", {"entities" : qUnion([Q0]), "transformType" : TransformType.TRANSLATION_3D, "dx" : 100 * mm, "dy" : 0 * mm, "dz" : 0 * mm, "makeCopy" : true});
        }
        {
            var Q0;
            Q0=makeQuery(id+"F81.opPattern","COPY",BODY,{"derivedFrom":makeQuery(id+"F80.opPattern","COPY",BODY,{"derivedFrom":makeQuery(id+"F79.opPattern","COPY",BODY,{"derivedFrom":makeQuery(id+"F56.opExtrude","SWEPT_BODY",BODY,{"disambiguationData":[OSD([sQuery(id+"F55.wireOp",EDGE,"E31.bottom"),sQuery(id+"F55.wireOp",EDGE,"E31.top"),sQuery(id+"F55.wireOp",EDGE,"E31.left"),sQuery(id+"F55.wireOp",EDGE,"E31.right")])]}),"instanceName":"1"}),"instanceName":"1"}),"instanceName":"1"});
            transform(context, id + "F82", {"entities" : qUnion([Q0]), "transformType" : TransformType.TRANSLATION_3D, "dx" : 100 * mm, "dy" : 0 * mm, "dz" : 0 * mm, "makeCopy" : true});
        }
        {
            var Q0;
            Q0=makeQuery(id+"F82.opPattern","COPY",BODY,{"derivedFrom":makeQuery(id+"F81.opPattern","COPY",BODY,{"derivedFrom":makeQuery(id+"F80.opPattern","COPY",BODY,{"derivedFrom":makeQuery(id+"F79.opPattern","COPY",BODY,{"derivedFrom":makeQuery(id+"F56.opExtrude","SWEPT_BODY",BODY,{"disambiguationData":[OSD([sQuery(id+"F55.wireOp",EDGE,"E31.bottom"),sQuery(id+"F55.wireOp",EDGE,"E31.top"),sQuery(id+"F55.wireOp",EDGE,"E31.left"),sQuery(id+"F55.wireOp",EDGE,"E31.right")])]}),"instanceName":"1"}),"instanceName":"1"}),"instanceName":"1"}),"instanceName":"1"});
            transform(context, id + "F83", {"entities" : qUnion([Q0]), "transformType" : TransformType.TRANSLATION_3D, "dx" : 100 * mm, "dy" : 0 * mm, "dz" : 0 * mm, "makeCopy" : true});
        }
        {
            var Q0;
            Q0=makeQuery(id+"F83.opPattern","COPY",BODY,{"derivedFrom":makeQuery(id+"F82.opPattern","COPY",BODY,{"derivedFrom":makeQuery(id+"F81.opPattern","COPY",BODY,{"derivedFrom":makeQuery(id+"F80.opPattern","COPY",BODY,{"derivedFrom":makeQuery(id+"F79.opPattern","COPY",BODY,{"derivedFrom":makeQuery(id+"F56.opExtrude","SWEPT_BODY",BODY,{"disambiguationData":[OSD([sQuery(id+"F55.wireOp",EDGE,"E31.bottom"),sQuery(id+"F55.wireOp",EDGE,"E31.top"),sQuery(id+"F55.wireOp",EDGE,"E31.left"),sQuery(id+"F55.wireOp",EDGE,"E31.right")])]}),"instanceName":"1"}),"instanceName":"1"}),"instanceName":"1"}),"instanceName":"1"}),"instanceName":"1"});
            transform(context, id + "F84", {"entities" : qUnion([Q0]), "transformType" : TransformType.TRANSLATION_3D, "dx" : 100 * mm, "dy" : 0 * mm, "dz" : 0 * mm, "makeCopy" : true});
        }
        {
            var Q0;
            Q0=makeQuery(id+"F84.opPattern","COPY",BODY,{"derivedFrom":makeQuery(id+"F83.opPattern","COPY",BODY,{"derivedFrom":makeQuery(id+"F82.opPattern","COPY",BODY,{"derivedFrom":makeQuery(id+"F81.opPattern","COPY",BODY,{"derivedFrom":makeQuery(id+"F80.opPattern","COPY",BODY,{"derivedFrom":makeQuery(id+"F79.opPattern","COPY",BODY,{"derivedFrom":makeQuery(id+"F56.opExtrude","SWEPT_BODY",BODY,{"disambiguationData":[OSD([sQuery(id+"F55.wireOp",EDGE,"E31.bottom"),sQuery(id+"F55.wireOp",EDGE,"E31.top"),sQuery(id+"F55.wireOp",EDGE,"E31.left"),sQuery(id+"F55.wireOp",EDGE,"E31.right")])]}),"instanceName":"1"}),"instanceName":"1"}),"instanceName":"1"}),"instanceName":"1"}),"instanceName":"1"}),"instanceName":"1"});
            transform(context, id + "F85", {"entities" : qUnion([Q0]), "transformType" : TransformType.TRANSLATION_3D, "dx" : 100 * mm, "dy" : 0 * mm, "dz" : 0 * mm, "makeCopy" : true});
        }
        {
            var Q0;
            Q0=makeQuery(id+"F85.opPattern","COPY",BODY,{"derivedFrom":makeQuery(id+"F84.opPattern","COPY",BODY,{"derivedFrom":makeQuery(id+"F83.opPattern","COPY",BODY,{"derivedFrom":makeQuery(id+"F82.opPattern","COPY",BODY,{"derivedFrom":makeQuery(id+"F81.opPattern","COPY",BODY,{"derivedFrom":makeQuery(id+"F80.opPattern","COPY",BODY,{"derivedFrom":makeQuery(id+"F79.opPattern","COPY",BODY,{"derivedFrom":makeQuery(id+"F56.opExtrude","SWEPT_BODY",BODY,{"disambiguationData":[OSD([sQuery(id+"F55.wireOp",EDGE,"E31.bottom"),sQuery(id+"F55.wireOp",EDGE,"E31.top"),sQuery(id+"F55.wireOp",EDGE,"E31.left"),sQuery(id+"F55.wireOp",EDGE,"E31.right")])]}),"instanceName":"1"}),"instanceName":"1"}),"instanceName":"1"}),"instanceName":"1"}),"instanceName":"1"}),"instanceName":"1"}),"instanceName":"1"});
            var Q1;
            Q1=makeQuery(id+"F84.opPattern","COPY",BODY,{"derivedFrom":makeQuery(id+"F83.opPattern","COPY",BODY,{"derivedFrom":makeQuery(id+"F82.opPattern","COPY",BODY,{"derivedFrom":makeQuery(id+"F81.opPattern","COPY",BODY,{"derivedFrom":makeQuery(id+"F80.opPattern","COPY",BODY,{"derivedFrom":makeQuery(id+"F79.opPattern","COPY",BODY,{"derivedFrom":makeQuery(id+"F56.opExtrude","SWEPT_BODY",BODY,{"disambiguationData":[OSD([sQuery(id+"F55.wireOp",EDGE,"E31.bottom"),sQuery(id+"F55.wireOp",EDGE,"E31.top"),sQuery(id+"F55.wireOp",EDGE,"E31.left"),sQuery(id+"F55.wireOp",EDGE,"E31.right")])]}),"instanceName":"1"}),"instanceName":"1"}),"instanceName":"1"}),"instanceName":"1"}),"instanceName":"1"}),"instanceName":"1"});
            var Q2;
            Q2=makeQuery(id+"F83.opPattern","COPY",BODY,{"derivedFrom":makeQuery(id+"F82.opPattern","COPY",BODY,{"derivedFrom":makeQuery(id+"F81.opPattern","COPY",BODY,{"derivedFrom":makeQuery(id+"F80.opPattern","COPY",BODY,{"derivedFrom":makeQuery(id+"F79.opPattern","COPY",BODY,{"derivedFrom":makeQuery(id+"F56.opExtrude","SWEPT_BODY",BODY,{"disambiguationData":[OSD([sQuery(id+"F55.wireOp",EDGE,"E31.bottom"),sQuery(id+"F55.wireOp",EDGE,"E31.top"),sQuery(id+"F55.wireOp",EDGE,"E31.left"),sQuery(id+"F55.wireOp",EDGE,"E31.right")])]}),"instanceName":"1"}),"instanceName":"1"}),"instanceName":"1"}),"instanceName":"1"}),"instanceName":"1"});
            var Q3;
            Q3=makeQuery(id+"F82.opPattern","COPY",BODY,{"derivedFrom":makeQuery(id+"F81.opPattern","COPY",BODY,{"derivedFrom":makeQuery(id+"F80.opPattern","COPY",BODY,{"derivedFrom":makeQuery(id+"F79.opPattern","COPY",BODY,{"derivedFrom":makeQuery(id+"F56.opExtrude","SWEPT_BODY",BODY,{"disambiguationData":[OSD([sQuery(id+"F55.wireOp",EDGE,"E31.bottom"),sQuery(id+"F55.wireOp",EDGE,"E31.top"),sQuery(id+"F55.wireOp",EDGE,"E31.left"),sQuery(id+"F55.wireOp",EDGE,"E31.right")])]}),"instanceName":"1"}),"instanceName":"1"}),"instanceName":"1"}),"instanceName":"1"});
            var Q4;
            Q4=makeQuery(id+"F81.opPattern","COPY",BODY,{"derivedFrom":makeQuery(id+"F80.opPattern","COPY",BODY,{"derivedFrom":makeQuery(id+"F79.opPattern","COPY",BODY,{"derivedFrom":makeQuery(id+"F56.opExtrude","SWEPT_BODY",BODY,{"disambiguationData":[OSD([sQuery(id+"F55.wireOp",EDGE,"E31.bottom"),sQuery(id+"F55.wireOp",EDGE,"E31.top"),sQuery(id+"F55.wireOp",EDGE,"E31.left"),sQuery(id+"F55.wireOp",EDGE,"E31.right")])]}),"instanceName":"1"}),"instanceName":"1"}),"instanceName":"1"});
            var Q5;
            Q5=makeQuery(id+"F80.opPattern","COPY",BODY,{"derivedFrom":makeQuery(id+"F79.opPattern","COPY",BODY,{"derivedFrom":makeQuery(id+"F56.opExtrude","SWEPT_BODY",BODY,{"disambiguationData":[OSD([sQuery(id+"F55.wireOp",EDGE,"E31.bottom"),sQuery(id+"F55.wireOp",EDGE,"E31.top"),sQuery(id+"F55.wireOp",EDGE,"E31.left"),sQuery(id+"F55.wireOp",EDGE,"E31.right")])]}),"instanceName":"1"}),"instanceName":"1"});
            var Q6;
            Q6=makeQuery(id+"F79.opPattern","COPY",BODY,{"derivedFrom":makeQuery(id+"F56.opExtrude","SWEPT_BODY",BODY,{"disambiguationData":[OSD([sQuery(id+"F55.wireOp",EDGE,"E31.bottom"),sQuery(id+"F55.wireOp",EDGE,"E31.top"),sQuery(id+"F55.wireOp",EDGE,"E31.left"),sQuery(id+"F55.wireOp",EDGE,"E31.right")])]}),"instanceName":"1"});
            transform(context, id + "F86", {"entities" : qUnion([Q0, Q1, Q2, Q3, Q4, Q5, Q6]), "transformType" : TransformType.TRANSLATION_3D, "dx" : 700 * mm, "dy" : 0 * mm, "dz" : 0 * mm, "makeCopy" : true});
        }
        {
            var Q0;
            Q0=makeQuery(id+"F86.opPattern","COPY",BODY,{"derivedFrom":makeQuery(id+"F85.opPattern","COPY",BODY,{"derivedFrom":makeQuery(id+"F84.opPattern","COPY",BODY,{"derivedFrom":makeQuery(id+"F83.opPattern","COPY",BODY,{"derivedFrom":makeQuery(id+"F82.opPattern","COPY",BODY,{"derivedFrom":makeQuery(id+"F81.opPattern","COPY",BODY,{"derivedFrom":makeQuery(id+"F80.opPattern","COPY",BODY,{"derivedFrom":makeQuery(id+"F79.opPattern","COPY",BODY,{"derivedFrom":makeQuery(id+"F56.opExtrude","SWEPT_BODY",BODY,{"disambiguationData":[OSD([sQuery(id+"F55.wireOp",EDGE,"E31.bottom"),sQuery(id+"F55.wireOp",EDGE,"E31.top"),sQuery(id+"F55.wireOp",EDGE,"E31.left"),sQuery(id+"F55.wireOp",EDGE,"E31.right")])]}),"instanceName":"1"}),"instanceName":"1"}),"instanceName":"1"}),"instanceName":"1"}),"instanceName":"1"}),"instanceName":"1"}),"instanceName":"1"}),"instanceName":"1"});
            var Q1;
            Q1=makeQuery(id+"F86.opPattern","COPY",BODY,{"derivedFrom":makeQuery(id+"F84.opPattern","COPY",BODY,{"derivedFrom":makeQuery(id+"F83.opPattern","COPY",BODY,{"derivedFrom":makeQuery(id+"F82.opPattern","COPY",BODY,{"derivedFrom":makeQuery(id+"F81.opPattern","COPY",BODY,{"derivedFrom":makeQuery(id+"F80.opPattern","COPY",BODY,{"derivedFrom":makeQuery(id+"F79.opPattern","COPY",BODY,{"derivedFrom":makeQuery(id+"F56.opExtrude","SWEPT_BODY",BODY,{"disambiguationData":[OSD([sQuery(id+"F55.wireOp",EDGE,"E31.bottom"),sQuery(id+"F55.wireOp",EDGE,"E31.top"),sQuery(id+"F55.wireOp",EDGE,"E31.left"),sQuery(id+"F55.wireOp",EDGE,"E31.right")])]}),"instanceName":"1"}),"instanceName":"1"}),"instanceName":"1"}),"instanceName":"1"}),"instanceName":"1"}),"instanceName":"1"}),"instanceName":"1"});
            var Q2;
            Q2=makeQuery(id+"F86.opPattern","COPY",BODY,{"derivedFrom":makeQuery(id+"F83.opPattern","COPY",BODY,{"derivedFrom":makeQuery(id+"F82.opPattern","COPY",BODY,{"derivedFrom":makeQuery(id+"F81.opPattern","COPY",BODY,{"derivedFrom":makeQuery(id+"F80.opPattern","COPY",BODY,{"derivedFrom":makeQuery(id+"F79.opPattern","COPY",BODY,{"derivedFrom":makeQuery(id+"F56.opExtrude","SWEPT_BODY",BODY,{"disambiguationData":[OSD([sQuery(id+"F55.wireOp",EDGE,"E31.bottom"),sQuery(id+"F55.wireOp",EDGE,"E31.top"),sQuery(id+"F55.wireOp",EDGE,"E31.left"),sQuery(id+"F55.wireOp",EDGE,"E31.right")])]}),"instanceName":"1"}),"instanceName":"1"}),"instanceName":"1"}),"instanceName":"1"}),"instanceName":"1"}),"instanceName":"1"});
            var Q3;
            Q3=makeQuery(id+"F86.opPattern","COPY",BODY,{"derivedFrom":makeQuery(id+"F82.opPattern","COPY",BODY,{"derivedFrom":makeQuery(id+"F81.opPattern","COPY",BODY,{"derivedFrom":makeQuery(id+"F80.opPattern","COPY",BODY,{"derivedFrom":makeQuery(id+"F79.opPattern","COPY",BODY,{"derivedFrom":makeQuery(id+"F56.opExtrude","SWEPT_BODY",BODY,{"disambiguationData":[OSD([sQuery(id+"F55.wireOp",EDGE,"E31.bottom"),sQuery(id+"F55.wireOp",EDGE,"E31.top"),sQuery(id+"F55.wireOp",EDGE,"E31.left"),sQuery(id+"F55.wireOp",EDGE,"E31.right")])]}),"instanceName":"1"}),"instanceName":"1"}),"instanceName":"1"}),"instanceName":"1"}),"instanceName":"1"});
            var Q4;
            Q4=makeQuery(id+"F86.opPattern","COPY",BODY,{"derivedFrom":makeQuery(id+"F81.opPattern","COPY",BODY,{"derivedFrom":makeQuery(id+"F80.opPattern","COPY",BODY,{"derivedFrom":makeQuery(id+"F79.opPattern","COPY",BODY,{"derivedFrom":makeQuery(id+"F56.opExtrude","SWEPT_BODY",BODY,{"disambiguationData":[OSD([sQuery(id+"F55.wireOp",EDGE,"E31.bottom"),sQuery(id+"F55.wireOp",EDGE,"E31.top"),sQuery(id+"F55.wireOp",EDGE,"E31.left"),sQuery(id+"F55.wireOp",EDGE,"E31.right")])]}),"instanceName":"1"}),"instanceName":"1"}),"instanceName":"1"}),"instanceName":"1"});
            var Q5;
            Q5=makeQuery(id+"F86.opPattern","COPY",BODY,{"derivedFrom":makeQuery(id+"F80.opPattern","COPY",BODY,{"derivedFrom":makeQuery(id+"F79.opPattern","COPY",BODY,{"derivedFrom":makeQuery(id+"F56.opExtrude","SWEPT_BODY",BODY,{"disambiguationData":[OSD([sQuery(id+"F55.wireOp",EDGE,"E31.bottom"),sQuery(id+"F55.wireOp",EDGE,"E31.top"),sQuery(id+"F55.wireOp",EDGE,"E31.left"),sQuery(id+"F55.wireOp",EDGE,"E31.right")])]}),"instanceName":"1"}),"instanceName":"1"}),"instanceName":"1"});
            var Q6;
            Q6=makeQuery(id+"F86.opPattern","COPY",BODY,{"derivedFrom":makeQuery(id+"F79.opPattern","COPY",BODY,{"derivedFrom":makeQuery(id+"F56.opExtrude","SWEPT_BODY",BODY,{"disambiguationData":[OSD([sQuery(id+"F55.wireOp",EDGE,"E31.bottom"),sQuery(id+"F55.wireOp",EDGE,"E31.top"),sQuery(id+"F55.wireOp",EDGE,"E31.left"),sQuery(id+"F55.wireOp",EDGE,"E31.right")])]}),"instanceName":"1"}),"instanceName":"1"});
            var Q7;
            Q7=makeQuery(id+"F85.opPattern","COPY",BODY,{"derivedFrom":makeQuery(id+"F84.opPattern","COPY",BODY,{"derivedFrom":makeQuery(id+"F83.opPattern","COPY",BODY,{"derivedFrom":makeQuery(id+"F82.opPattern","COPY",BODY,{"derivedFrom":makeQuery(id+"F81.opPattern","COPY",BODY,{"derivedFrom":makeQuery(id+"F80.opPattern","COPY",BODY,{"derivedFrom":makeQuery(id+"F79.opPattern","COPY",BODY,{"derivedFrom":makeQuery(id+"F56.opExtrude","SWEPT_BODY",BODY,{"disambiguationData":[OSD([sQuery(id+"F55.wireOp",EDGE,"E31.bottom"),sQuery(id+"F55.wireOp",EDGE,"E31.top"),sQuery(id+"F55.wireOp",EDGE,"E31.left"),sQuery(id+"F55.wireOp",EDGE,"E31.right")])]}),"instanceName":"1"}),"instanceName":"1"}),"instanceName":"1"}),"instanceName":"1"}),"instanceName":"1"}),"instanceName":"1"}),"instanceName":"1"});
            var Q8;
            Q8=makeQuery(id+"F84.opPattern","COPY",BODY,{"derivedFrom":makeQuery(id+"F83.opPattern","COPY",BODY,{"derivedFrom":makeQuery(id+"F82.opPattern","COPY",BODY,{"derivedFrom":makeQuery(id+"F81.opPattern","COPY",BODY,{"derivedFrom":makeQuery(id+"F80.opPattern","COPY",BODY,{"derivedFrom":makeQuery(id+"F79.opPattern","COPY",BODY,{"derivedFrom":makeQuery(id+"F56.opExtrude","SWEPT_BODY",BODY,{"disambiguationData":[OSD([sQuery(id+"F55.wireOp",EDGE,"E31.bottom"),sQuery(id+"F55.wireOp",EDGE,"E31.top"),sQuery(id+"F55.wireOp",EDGE,"E31.left"),sQuery(id+"F55.wireOp",EDGE,"E31.right")])]}),"instanceName":"1"}),"instanceName":"1"}),"instanceName":"1"}),"instanceName":"1"}),"instanceName":"1"}),"instanceName":"1"});
            var Q9;
            Q9=makeQuery(id+"F83.opPattern","COPY",BODY,{"derivedFrom":makeQuery(id+"F82.opPattern","COPY",BODY,{"derivedFrom":makeQuery(id+"F81.opPattern","COPY",BODY,{"derivedFrom":makeQuery(id+"F80.opPattern","COPY",BODY,{"derivedFrom":makeQuery(id+"F79.opPattern","COPY",BODY,{"derivedFrom":makeQuery(id+"F56.opExtrude","SWEPT_BODY",BODY,{"disambiguationData":[OSD([sQuery(id+"F55.wireOp",EDGE,"E31.bottom"),sQuery(id+"F55.wireOp",EDGE,"E31.top"),sQuery(id+"F55.wireOp",EDGE,"E31.left"),sQuery(id+"F55.wireOp",EDGE,"E31.right")])]}),"instanceName":"1"}),"instanceName":"1"}),"instanceName":"1"}),"instanceName":"1"}),"instanceName":"1"});
            var Q10;
            Q10=makeQuery(id+"F82.opPattern","COPY",BODY,{"derivedFrom":makeQuery(id+"F81.opPattern","COPY",BODY,{"derivedFrom":makeQuery(id+"F80.opPattern","COPY",BODY,{"derivedFrom":makeQuery(id+"F79.opPattern","COPY",BODY,{"derivedFrom":makeQuery(id+"F56.opExtrude","SWEPT_BODY",BODY,{"disambiguationData":[OSD([sQuery(id+"F55.wireOp",EDGE,"E31.bottom"),sQuery(id+"F55.wireOp",EDGE,"E31.top"),sQuery(id+"F55.wireOp",EDGE,"E31.left"),sQuery(id+"F55.wireOp",EDGE,"E31.right")])]}),"instanceName":"1"}),"instanceName":"1"}),"instanceName":"1"}),"instanceName":"1"});
            transform(context, id + "F87", {"entities" : qUnion([Q0, Q1, Q2, Q3, Q4, Q5, Q6, Q7, Q8, Q9, Q10]), "transformType" : TransformType.TRANSLATION_3D, "dx" : 1100 * mm, "dy" : 0 * mm, "dz" : 0 * mm, "makeCopy" : true});
        }
        {
            var Q0;
            Q0=makeQuery(id+"F21.opExtrude","SWEPT_BODY",BODY,{"disambiguationData":[OSD([sQuery(id+"F20.wireOp",EDGE,"E13"),sQuery(id+"F20.wireOp",EDGE,"E15"),sQuery(id+"F20.wireOp",EDGE,"E17.bottom"),sQuery(id+"F20.wireOp",EDGE,"E17.right"),sQuery(id+"F20.wireOp",EDGE,"4LeHWZBI-6k9Y-MK96-v7Qf-pvXBpWzVvBlG.bottom"),sQuery(id+"F20.wireOp",EDGE,"4LeHWZBI-6k9Y-MK96-v7Qf-pvXBpWzVvBlG.top"),sQuery(id+"F20.wireOp",EDGE,"E14"),sQuery(id+"F20.wireOp",EDGE,"4LeHWZBI-6k9Y-MK96-v7Qf-pvXBpWzVvBlG.right"),sQuery(id+"F20.wireOp",EDGE,"E18.top"),sQuery(id+"F20.wireOp",EDGE,"E18.left"),sQuery(id+"F20.wireOp",EDGE,"E18.right")])]});
            var Q1;
            Q1=makeQuery(id+"F12.opPattern","COPY",BODY,{"derivedFrom":makeQuery(id+"F10.opExtrude","SWEPT_BODY",BODY,{"disambiguationData":[OSD([sQuery(id+"F9.wireOp",EDGE,"E12.bottom"),sQuery(id+"F9.wireOp",EDGE,"E12.top"),sQuery(id+"F9.wireOp",EDGE,"E12.left"),sQuery(id+"F9.wireOp",EDGE,"E12.right")])]}),"instanceName":"1"});
            var Q2;
            Q2=makeQuery(id+"F13.opPattern","COPY",BODY,{"derivedFrom":makeQuery(id+"F12.opPattern","COPY",BODY,{"derivedFrom":makeQuery(id+"F10.opExtrude","SWEPT_BODY",BODY,{"disambiguationData":[OSD([sQuery(id+"F9.wireOp",EDGE,"E12.bottom"),sQuery(id+"F9.wireOp",EDGE,"E12.top"),sQuery(id+"F9.wireOp",EDGE,"E12.left"),sQuery(id+"F9.wireOp",EDGE,"E12.right")])]}),"instanceName":"1"}),"instanceName":"1"});
            var Q3;
            Q3=makeQuery(id+"F14.opPattern","COPY",BODY,{"derivedFrom":makeQuery(id+"F13.opPattern","COPY",BODY,{"derivedFrom":makeQuery(id+"F12.opPattern","COPY",BODY,{"derivedFrom":makeQuery(id+"F10.opExtrude","SWEPT_BODY",BODY,{"disambiguationData":[OSD([sQuery(id+"F9.wireOp",EDGE,"E12.bottom"),sQuery(id+"F9.wireOp",EDGE,"E12.top"),sQuery(id+"F9.wireOp",EDGE,"E12.left"),sQuery(id+"F9.wireOp",EDGE,"E12.right")])]}),"instanceName":"1"}),"instanceName":"1"}),"instanceName":"1"});
            var Q4;
            Q4=makeQuery(id+"F16.opPattern","COPY",BODY,{"derivedFrom":makeQuery(id+"F12.opPattern","COPY",BODY,{"derivedFrom":makeQuery(id+"F10.opExtrude","SWEPT_BODY",BODY,{"disambiguationData":[OSD([sQuery(id+"F9.wireOp",EDGE,"E12.bottom"),sQuery(id+"F9.wireOp",EDGE,"E12.top"),sQuery(id+"F9.wireOp",EDGE,"E12.left"),sQuery(id+"F9.wireOp",EDGE,"E12.right")])]}),"instanceName":"1"}),"instanceName":"1"});
            var Q5;
            Q5=makeQuery(id+"F17.opPattern","COPY",BODY,{"derivedFrom":makeQuery(id+"F10.opExtrude","SWEPT_BODY",BODY,{"disambiguationData":[OSD([sQuery(id+"F9.wireOp",EDGE,"E12.bottom"),sQuery(id+"F9.wireOp",EDGE,"E12.top"),sQuery(id+"F9.wireOp",EDGE,"E12.left"),sQuery(id+"F9.wireOp",EDGE,"E12.right")])]}),"instanceName":"1"});
            var Q6;
            Q6=makeQuery(id+"F18.opPattern","COPY",BODY,{"derivedFrom":makeQuery(id+"F17.opPattern","COPY",BODY,{"derivedFrom":makeQuery(id+"F10.opExtrude","SWEPT_BODY",BODY,{"disambiguationData":[OSD([sQuery(id+"F9.wireOp",EDGE,"E12.bottom"),sQuery(id+"F9.wireOp",EDGE,"E12.top"),sQuery(id+"F9.wireOp",EDGE,"E12.left"),sQuery(id+"F9.wireOp",EDGE,"E12.right")])]}),"instanceName":"1"}),"instanceName":"1"});
            var Q7;
            Q7=makeQuery(id+"F19.opPattern","COPY",BODY,{"derivedFrom":makeQuery(id+"F18.opPattern","COPY",BODY,{"derivedFrom":makeQuery(id+"F17.opPattern","COPY",BODY,{"derivedFrom":makeQuery(id+"F10.opExtrude","SWEPT_BODY",BODY,{"disambiguationData":[OSD([sQuery(id+"F9.wireOp",EDGE,"E12.bottom"),sQuery(id+"F9.wireOp",EDGE,"E12.top"),sQuery(id+"F9.wireOp",EDGE,"E12.left"),sQuery(id+"F9.wireOp",EDGE,"E12.right")])]}),"instanceName":"1"}),"instanceName":"1"}),"instanceName":"1"});
            var Q8;
            Q8=makeQuery(id+"F79.opPattern","COPY",BODY,{"derivedFrom":makeQuery(id+"F56.opExtrude","SWEPT_BODY",BODY,{"disambiguationData":[OSD([sQuery(id+"F55.wireOp",EDGE,"E31.bottom"),sQuery(id+"F55.wireOp",EDGE,"E31.top"),sQuery(id+"F55.wireOp",EDGE,"E31.left"),sQuery(id+"F55.wireOp",EDGE,"E31.right")])]}),"instanceName":"1"});
            var Q9;
            Q9=makeQuery(id+"F80.opPattern","COPY",BODY,{"derivedFrom":makeQuery(id+"F79.opPattern","COPY",BODY,{"derivedFrom":makeQuery(id+"F56.opExtrude","SWEPT_BODY",BODY,{"disambiguationData":[OSD([sQuery(id+"F55.wireOp",EDGE,"E31.bottom"),sQuery(id+"F55.wireOp",EDGE,"E31.top"),sQuery(id+"F55.wireOp",EDGE,"E31.left"),sQuery(id+"F55.wireOp",EDGE,"E31.right")])]}),"instanceName":"1"}),"instanceName":"1"});
            var Q10;
            Q10=makeQuery(id+"F81.opPattern","COPY",BODY,{"derivedFrom":makeQuery(id+"F80.opPattern","COPY",BODY,{"derivedFrom":makeQuery(id+"F79.opPattern","COPY",BODY,{"derivedFrom":makeQuery(id+"F56.opExtrude","SWEPT_BODY",BODY,{"disambiguationData":[OSD([sQuery(id+"F55.wireOp",EDGE,"E31.bottom"),sQuery(id+"F55.wireOp",EDGE,"E31.top"),sQuery(id+"F55.wireOp",EDGE,"E31.left"),sQuery(id+"F55.wireOp",EDGE,"E31.right")])]}),"instanceName":"1"}),"instanceName":"1"}),"instanceName":"1"});
            var Q11;
            Q11=makeQuery(id+"F82.opPattern","COPY",BODY,{"derivedFrom":makeQuery(id+"F81.opPattern","COPY",BODY,{"derivedFrom":makeQuery(id+"F80.opPattern","COPY",BODY,{"derivedFrom":makeQuery(id+"F79.opPattern","COPY",BODY,{"derivedFrom":makeQuery(id+"F56.opExtrude","SWEPT_BODY",BODY,{"disambiguationData":[OSD([sQuery(id+"F55.wireOp",EDGE,"E31.bottom"),sQuery(id+"F55.wireOp",EDGE,"E31.top"),sQuery(id+"F55.wireOp",EDGE,"E31.left"),sQuery(id+"F55.wireOp",EDGE,"E31.right")])]}),"instanceName":"1"}),"instanceName":"1"}),"instanceName":"1"}),"instanceName":"1"});
            var Q12;
            Q12=makeQuery(id+"F83.opPattern","COPY",BODY,{"derivedFrom":makeQuery(id+"F82.opPattern","COPY",BODY,{"derivedFrom":makeQuery(id+"F81.opPattern","COPY",BODY,{"derivedFrom":makeQuery(id+"F80.opPattern","COPY",BODY,{"derivedFrom":makeQuery(id+"F79.opPattern","COPY",BODY,{"derivedFrom":makeQuery(id+"F56.opExtrude","SWEPT_BODY",BODY,{"disambiguationData":[OSD([sQuery(id+"F55.wireOp",EDGE,"E31.bottom"),sQuery(id+"F55.wireOp",EDGE,"E31.top"),sQuery(id+"F55.wireOp",EDGE,"E31.left"),sQuery(id+"F55.wireOp",EDGE,"E31.right")])]}),"instanceName":"1"}),"instanceName":"1"}),"instanceName":"1"}),"instanceName":"1"}),"instanceName":"1"});
            var Q13;
            Q13=makeQuery(id+"F84.opPattern","COPY",BODY,{"derivedFrom":makeQuery(id+"F83.opPattern","COPY",BODY,{"derivedFrom":makeQuery(id+"F82.opPattern","COPY",BODY,{"derivedFrom":makeQuery(id+"F81.opPattern","COPY",BODY,{"derivedFrom":makeQuery(id+"F80.opPattern","COPY",BODY,{"derivedFrom":makeQuery(id+"F79.opPattern","COPY",BODY,{"derivedFrom":makeQuery(id+"F56.opExtrude","SWEPT_BODY",BODY,{"disambiguationData":[OSD([sQuery(id+"F55.wireOp",EDGE,"E31.bottom"),sQuery(id+"F55.wireOp",EDGE,"E31.top"),sQuery(id+"F55.wireOp",EDGE,"E31.left"),sQuery(id+"F55.wireOp",EDGE,"E31.right")])]}),"instanceName":"1"}),"instanceName":"1"}),"instanceName":"1"}),"instanceName":"1"}),"instanceName":"1"}),"instanceName":"1"});
            var Q14;
            Q14=makeQuery(id+"F85.opPattern","COPY",BODY,{"derivedFrom":makeQuery(id+"F84.opPattern","COPY",BODY,{"derivedFrom":makeQuery(id+"F83.opPattern","COPY",BODY,{"derivedFrom":makeQuery(id+"F82.opPattern","COPY",BODY,{"derivedFrom":makeQuery(id+"F81.opPattern","COPY",BODY,{"derivedFrom":makeQuery(id+"F80.opPattern","COPY",BODY,{"derivedFrom":makeQuery(id+"F79.opPattern","COPY",BODY,{"derivedFrom":makeQuery(id+"F56.opExtrude","SWEPT_BODY",BODY,{"disambiguationData":[OSD([sQuery(id+"F55.wireOp",EDGE,"E31.bottom"),sQuery(id+"F55.wireOp",EDGE,"E31.top"),sQuery(id+"F55.wireOp",EDGE,"E31.left"),sQuery(id+"F55.wireOp",EDGE,"E31.right")])]}),"instanceName":"1"}),"instanceName":"1"}),"instanceName":"1"}),"instanceName":"1"}),"instanceName":"1"}),"instanceName":"1"}),"instanceName":"1"});
            var Q15;
            Q15=makeQuery(id+"F86.opPattern","COPY",BODY,{"derivedFrom":makeQuery(id+"F79.opPattern","COPY",BODY,{"derivedFrom":makeQuery(id+"F56.opExtrude","SWEPT_BODY",BODY,{"disambiguationData":[OSD([sQuery(id+"F55.wireOp",EDGE,"E31.bottom"),sQuery(id+"F55.wireOp",EDGE,"E31.top"),sQuery(id+"F55.wireOp",EDGE,"E31.left"),sQuery(id+"F55.wireOp",EDGE,"E31.right")])]}),"instanceName":"1"}),"instanceName":"1"});
            var Q16;
            Q16=makeQuery(id+"F86.opPattern","COPY",BODY,{"derivedFrom":makeQuery(id+"F80.opPattern","COPY",BODY,{"derivedFrom":makeQuery(id+"F79.opPattern","COPY",BODY,{"derivedFrom":makeQuery(id+"F56.opExtrude","SWEPT_BODY",BODY,{"disambiguationData":[OSD([sQuery(id+"F55.wireOp",EDGE,"E31.bottom"),sQuery(id+"F55.wireOp",EDGE,"E31.top"),sQuery(id+"F55.wireOp",EDGE,"E31.left"),sQuery(id+"F55.wireOp",EDGE,"E31.right")])]}),"instanceName":"1"}),"instanceName":"1"}),"instanceName":"1"});
            var Q17;
            Q17=makeQuery(id+"F86.opPattern","COPY",BODY,{"derivedFrom":makeQuery(id+"F81.opPattern","COPY",BODY,{"derivedFrom":makeQuery(id+"F80.opPattern","COPY",BODY,{"derivedFrom":makeQuery(id+"F79.opPattern","COPY",BODY,{"derivedFrom":makeQuery(id+"F56.opExtrude","SWEPT_BODY",BODY,{"disambiguationData":[OSD([sQuery(id+"F55.wireOp",EDGE,"E31.bottom"),sQuery(id+"F55.wireOp",EDGE,"E31.top"),sQuery(id+"F55.wireOp",EDGE,"E31.left"),sQuery(id+"F55.wireOp",EDGE,"E31.right")])]}),"instanceName":"1"}),"instanceName":"1"}),"instanceName":"1"}),"instanceName":"1"});
            var Q18;
            Q18=makeQuery(id+"F86.opPattern","COPY",BODY,{"derivedFrom":makeQuery(id+"F82.opPattern","COPY",BODY,{"derivedFrom":makeQuery(id+"F81.opPattern","COPY",BODY,{"derivedFrom":makeQuery(id+"F80.opPattern","COPY",BODY,{"derivedFrom":makeQuery(id+"F79.opPattern","COPY",BODY,{"derivedFrom":makeQuery(id+"F56.opExtrude","SWEPT_BODY",BODY,{"disambiguationData":[OSD([sQuery(id+"F55.wireOp",EDGE,"E31.bottom"),sQuery(id+"F55.wireOp",EDGE,"E31.top"),sQuery(id+"F55.wireOp",EDGE,"E31.left"),sQuery(id+"F55.wireOp",EDGE,"E31.right")])]}),"instanceName":"1"}),"instanceName":"1"}),"instanceName":"1"}),"instanceName":"1"}),"instanceName":"1"});
            var Q19;
            Q19=makeQuery(id+"F86.opPattern","COPY",BODY,{"derivedFrom":makeQuery(id+"F83.opPattern","COPY",BODY,{"derivedFrom":makeQuery(id+"F82.opPattern","COPY",BODY,{"derivedFrom":makeQuery(id+"F81.opPattern","COPY",BODY,{"derivedFrom":makeQuery(id+"F80.opPattern","COPY",BODY,{"derivedFrom":makeQuery(id+"F79.opPattern","COPY",BODY,{"derivedFrom":makeQuery(id+"F56.opExtrude","SWEPT_BODY",BODY,{"disambiguationData":[OSD([sQuery(id+"F55.wireOp",EDGE,"E31.bottom"),sQuery(id+"F55.wireOp",EDGE,"E31.top"),sQuery(id+"F55.wireOp",EDGE,"E31.left"),sQuery(id+"F55.wireOp",EDGE,"E31.right")])]}),"instanceName":"1"}),"instanceName":"1"}),"instanceName":"1"}),"instanceName":"1"}),"instanceName":"1"}),"instanceName":"1"});
            var Q20;
            Q20=makeQuery(id+"F86.opPattern","COPY",BODY,{"derivedFrom":makeQuery(id+"F84.opPattern","COPY",BODY,{"derivedFrom":makeQuery(id+"F83.opPattern","COPY",BODY,{"derivedFrom":makeQuery(id+"F82.opPattern","COPY",BODY,{"derivedFrom":makeQuery(id+"F81.opPattern","COPY",BODY,{"derivedFrom":makeQuery(id+"F80.opPattern","COPY",BODY,{"derivedFrom":makeQuery(id+"F79.opPattern","COPY",BODY,{"derivedFrom":makeQuery(id+"F56.opExtrude","SWEPT_BODY",BODY,{"disambiguationData":[OSD([sQuery(id+"F55.wireOp",EDGE,"E31.bottom"),sQuery(id+"F55.wireOp",EDGE,"E31.top"),sQuery(id+"F55.wireOp",EDGE,"E31.left"),sQuery(id+"F55.wireOp",EDGE,"E31.right")])]}),"instanceName":"1"}),"instanceName":"1"}),"instanceName":"1"}),"instanceName":"1"}),"instanceName":"1"}),"instanceName":"1"}),"instanceName":"1"});
            var Q21;
            Q21=makeQuery(id+"F86.opPattern","COPY",BODY,{"derivedFrom":makeQuery(id+"F85.opPattern","COPY",BODY,{"derivedFrom":makeQuery(id+"F84.opPattern","COPY",BODY,{"derivedFrom":makeQuery(id+"F83.opPattern","COPY",BODY,{"derivedFrom":makeQuery(id+"F82.opPattern","COPY",BODY,{"derivedFrom":makeQuery(id+"F81.opPattern","COPY",BODY,{"derivedFrom":makeQuery(id+"F80.opPattern","COPY",BODY,{"derivedFrom":makeQuery(id+"F79.opPattern","COPY",BODY,{"derivedFrom":makeQuery(id+"F56.opExtrude","SWEPT_BODY",BODY,{"disambiguationData":[OSD([sQuery(id+"F55.wireOp",EDGE,"E31.bottom"),sQuery(id+"F55.wireOp",EDGE,"E31.top"),sQuery(id+"F55.wireOp",EDGE,"E31.left"),sQuery(id+"F55.wireOp",EDGE,"E31.right")])]}),"instanceName":"1"}),"instanceName":"1"}),"instanceName":"1"}),"instanceName":"1"}),"instanceName":"1"}),"instanceName":"1"}),"instanceName":"1"}),"instanceName":"1"});
            var Q22;
            Q22=makeQuery(id+"F87.opPattern","COPY",BODY,{"derivedFrom":makeQuery(id+"F82.opPattern","COPY",BODY,{"derivedFrom":makeQuery(id+"F81.opPattern","COPY",BODY,{"derivedFrom":makeQuery(id+"F80.opPattern","COPY",BODY,{"derivedFrom":makeQuery(id+"F79.opPattern","COPY",BODY,{"derivedFrom":makeQuery(id+"F56.opExtrude","SWEPT_BODY",BODY,{"disambiguationData":[OSD([sQuery(id+"F55.wireOp",EDGE,"E31.bottom"),sQuery(id+"F55.wireOp",EDGE,"E31.top"),sQuery(id+"F55.wireOp",EDGE,"E31.left"),sQuery(id+"F55.wireOp",EDGE,"E31.right")])]}),"instanceName":"1"}),"instanceName":"1"}),"instanceName":"1"}),"instanceName":"1"}),"instanceName":"1"});
            var Q23;
            Q23=makeQuery(id+"F87.opPattern","COPY",BODY,{"derivedFrom":makeQuery(id+"F83.opPattern","COPY",BODY,{"derivedFrom":makeQuery(id+"F82.opPattern","COPY",BODY,{"derivedFrom":makeQuery(id+"F81.opPattern","COPY",BODY,{"derivedFrom":makeQuery(id+"F80.opPattern","COPY",BODY,{"derivedFrom":makeQuery(id+"F79.opPattern","COPY",BODY,{"derivedFrom":makeQuery(id+"F56.opExtrude","SWEPT_BODY",BODY,{"disambiguationData":[OSD([sQuery(id+"F55.wireOp",EDGE,"E31.bottom"),sQuery(id+"F55.wireOp",EDGE,"E31.top"),sQuery(id+"F55.wireOp",EDGE,"E31.left"),sQuery(id+"F55.wireOp",EDGE,"E31.right")])]}),"instanceName":"1"}),"instanceName":"1"}),"instanceName":"1"}),"instanceName":"1"}),"instanceName":"1"}),"instanceName":"1"});
            var Q24;
            Q24=makeQuery(id+"F87.opPattern","COPY",BODY,{"derivedFrom":makeQuery(id+"F84.opPattern","COPY",BODY,{"derivedFrom":makeQuery(id+"F83.opPattern","COPY",BODY,{"derivedFrom":makeQuery(id+"F82.opPattern","COPY",BODY,{"derivedFrom":makeQuery(id+"F81.opPattern","COPY",BODY,{"derivedFrom":makeQuery(id+"F80.opPattern","COPY",BODY,{"derivedFrom":makeQuery(id+"F79.opPattern","COPY",BODY,{"derivedFrom":makeQuery(id+"F56.opExtrude","SWEPT_BODY",BODY,{"disambiguationData":[OSD([sQuery(id+"F55.wireOp",EDGE,"E31.bottom"),sQuery(id+"F55.wireOp",EDGE,"E31.top"),sQuery(id+"F55.wireOp",EDGE,"E31.left"),sQuery(id+"F55.wireOp",EDGE,"E31.right")])]}),"instanceName":"1"}),"instanceName":"1"}),"instanceName":"1"}),"instanceName":"1"}),"instanceName":"1"}),"instanceName":"1"}),"instanceName":"1"});
            var Q25;
            Q25=makeQuery(id+"F87.opPattern","COPY",BODY,{"derivedFrom":makeQuery(id+"F85.opPattern","COPY",BODY,{"derivedFrom":makeQuery(id+"F84.opPattern","COPY",BODY,{"derivedFrom":makeQuery(id+"F83.opPattern","COPY",BODY,{"derivedFrom":makeQuery(id+"F82.opPattern","COPY",BODY,{"derivedFrom":makeQuery(id+"F81.opPattern","COPY",BODY,{"derivedFrom":makeQuery(id+"F80.opPattern","COPY",BODY,{"derivedFrom":makeQuery(id+"F79.opPattern","COPY",BODY,{"derivedFrom":makeQuery(id+"F56.opExtrude","SWEPT_BODY",BODY,{"disambiguationData":[OSD([sQuery(id+"F55.wireOp",EDGE,"E31.bottom"),sQuery(id+"F55.wireOp",EDGE,"E31.top"),sQuery(id+"F55.wireOp",EDGE,"E31.left"),sQuery(id+"F55.wireOp",EDGE,"E31.right")])]}),"instanceName":"1"}),"instanceName":"1"}),"instanceName":"1"}),"instanceName":"1"}),"instanceName":"1"}),"instanceName":"1"}),"instanceName":"1"}),"instanceName":"1"});
            var Q26;
            Q26=makeQuery(id+"F87.opPattern","COPY",BODY,{"derivedFrom":makeQuery(id+"F86.opPattern","COPY",BODY,{"derivedFrom":makeQuery(id+"F79.opPattern","COPY",BODY,{"derivedFrom":makeQuery(id+"F56.opExtrude","SWEPT_BODY",BODY,{"disambiguationData":[OSD([sQuery(id+"F55.wireOp",EDGE,"E31.bottom"),sQuery(id+"F55.wireOp",EDGE,"E31.top"),sQuery(id+"F55.wireOp",EDGE,"E31.left"),sQuery(id+"F55.wireOp",EDGE,"E31.right")])]}),"instanceName":"1"}),"instanceName":"1"}),"instanceName":"1"});
            var Q27;
            Q27=makeQuery(id+"F87.opPattern","COPY",BODY,{"derivedFrom":makeQuery(id+"F86.opPattern","COPY",BODY,{"derivedFrom":makeQuery(id+"F80.opPattern","COPY",BODY,{"derivedFrom":makeQuery(id+"F79.opPattern","COPY",BODY,{"derivedFrom":makeQuery(id+"F56.opExtrude","SWEPT_BODY",BODY,{"disambiguationData":[OSD([sQuery(id+"F55.wireOp",EDGE,"E31.bottom"),sQuery(id+"F55.wireOp",EDGE,"E31.top"),sQuery(id+"F55.wireOp",EDGE,"E31.left"),sQuery(id+"F55.wireOp",EDGE,"E31.right")])]}),"instanceName":"1"}),"instanceName":"1"}),"instanceName":"1"}),"instanceName":"1"});
            var Q28;
            Q28=makeQuery(id+"F87.opPattern","COPY",BODY,{"derivedFrom":makeQuery(id+"F86.opPattern","COPY",BODY,{"derivedFrom":makeQuery(id+"F81.opPattern","COPY",BODY,{"derivedFrom":makeQuery(id+"F80.opPattern","COPY",BODY,{"derivedFrom":makeQuery(id+"F79.opPattern","COPY",BODY,{"derivedFrom":makeQuery(id+"F56.opExtrude","SWEPT_BODY",BODY,{"disambiguationData":[OSD([sQuery(id+"F55.wireOp",EDGE,"E31.bottom"),sQuery(id+"F55.wireOp",EDGE,"E31.top"),sQuery(id+"F55.wireOp",EDGE,"E31.left"),sQuery(id+"F55.wireOp",EDGE,"E31.right")])]}),"instanceName":"1"}),"instanceName":"1"}),"instanceName":"1"}),"instanceName":"1"}),"instanceName":"1"});
            var Q29;
            Q29=makeQuery(id+"F87.opPattern","COPY",BODY,{"derivedFrom":makeQuery(id+"F86.opPattern","COPY",BODY,{"derivedFrom":makeQuery(id+"F82.opPattern","COPY",BODY,{"derivedFrom":makeQuery(id+"F81.opPattern","COPY",BODY,{"derivedFrom":makeQuery(id+"F80.opPattern","COPY",BODY,{"derivedFrom":makeQuery(id+"F79.opPattern","COPY",BODY,{"derivedFrom":makeQuery(id+"F56.opExtrude","SWEPT_BODY",BODY,{"disambiguationData":[OSD([sQuery(id+"F55.wireOp",EDGE,"E31.bottom"),sQuery(id+"F55.wireOp",EDGE,"E31.top"),sQuery(id+"F55.wireOp",EDGE,"E31.left"),sQuery(id+"F55.wireOp",EDGE,"E31.right")])]}),"instanceName":"1"}),"instanceName":"1"}),"instanceName":"1"}),"instanceName":"1"}),"instanceName":"1"}),"instanceName":"1"});
            var Q30;
            Q30=makeQuery(id+"F87.opPattern","COPY",BODY,{"derivedFrom":makeQuery(id+"F86.opPattern","COPY",BODY,{"derivedFrom":makeQuery(id+"F83.opPattern","COPY",BODY,{"derivedFrom":makeQuery(id+"F82.opPattern","COPY",BODY,{"derivedFrom":makeQuery(id+"F81.opPattern","COPY",BODY,{"derivedFrom":makeQuery(id+"F80.opPattern","COPY",BODY,{"derivedFrom":makeQuery(id+"F79.opPattern","COPY",BODY,{"derivedFrom":makeQuery(id+"F56.opExtrude","SWEPT_BODY",BODY,{"disambiguationData":[OSD([sQuery(id+"F55.wireOp",EDGE,"E31.bottom"),sQuery(id+"F55.wireOp",EDGE,"E31.top"),sQuery(id+"F55.wireOp",EDGE,"E31.left"),sQuery(id+"F55.wireOp",EDGE,"E31.right")])]}),"instanceName":"1"}),"instanceName":"1"}),"instanceName":"1"}),"instanceName":"1"}),"instanceName":"1"}),"instanceName":"1"}),"instanceName":"1"});
            var Q31;
            Q31=makeQuery(id+"F87.opPattern","COPY",BODY,{"derivedFrom":makeQuery(id+"F86.opPattern","COPY",BODY,{"derivedFrom":makeQuery(id+"F84.opPattern","COPY",BODY,{"derivedFrom":makeQuery(id+"F83.opPattern","COPY",BODY,{"derivedFrom":makeQuery(id+"F82.opPattern","COPY",BODY,{"derivedFrom":makeQuery(id+"F81.opPattern","COPY",BODY,{"derivedFrom":makeQuery(id+"F80.opPattern","COPY",BODY,{"derivedFrom":makeQuery(id+"F79.opPattern","COPY",BODY,{"derivedFrom":makeQuery(id+"F56.opExtrude","SWEPT_BODY",BODY,{"disambiguationData":[OSD([sQuery(id+"F55.wireOp",EDGE,"E31.bottom"),sQuery(id+"F55.wireOp",EDGE,"E31.top"),sQuery(id+"F55.wireOp",EDGE,"E31.left"),sQuery(id+"F55.wireOp",EDGE,"E31.right")])]}),"instanceName":"1"}),"instanceName":"1"}),"instanceName":"1"}),"instanceName":"1"}),"instanceName":"1"}),"instanceName":"1"}),"instanceName":"1"}),"instanceName":"1"});
            var Q32;
            Q32=makeQuery(id+"F87.opPattern","COPY",BODY,{"derivedFrom":makeQuery(id+"F86.opPattern","COPY",BODY,{"derivedFrom":makeQuery(id+"F85.opPattern","COPY",BODY,{"derivedFrom":makeQuery(id+"F84.opPattern","COPY",BODY,{"derivedFrom":makeQuery(id+"F83.opPattern","COPY",BODY,{"derivedFrom":makeQuery(id+"F82.opPattern","COPY",BODY,{"derivedFrom":makeQuery(id+"F81.opPattern","COPY",BODY,{"derivedFrom":makeQuery(id+"F80.opPattern","COPY",BODY,{"derivedFrom":makeQuery(id+"F79.opPattern","COPY",BODY,{"derivedFrom":makeQuery(id+"F56.opExtrude","SWEPT_BODY",BODY,{"disambiguationData":[OSD([sQuery(id+"F55.wireOp",EDGE,"E31.bottom"),sQuery(id+"F55.wireOp",EDGE,"E31.top"),sQuery(id+"F55.wireOp",EDGE,"E31.left"),sQuery(id+"F55.wireOp",EDGE,"E31.right")])]}),"instanceName":"1"}),"instanceName":"1"}),"instanceName":"1"}),"instanceName":"1"}),"instanceName":"1"}),"instanceName":"1"}),"instanceName":"1"}),"instanceName":"1"}),"instanceName":"1"});
            var Q33;
            Q33=makeQuery(id+"F72.opPattern","COPY",BODY,{"derivedFrom":makeQuery(id+"F71.opPattern","COPY",BODY,{"derivedFrom":makeQuery(id+"F70.opPattern","COPY",BODY,{"derivedFrom":makeQuery(id+"F69.opPattern","COPY",BODY,{"derivedFrom":makeQuery(id+"F68.opPattern","COPY",BODY,{"derivedFrom":makeQuery(id+"F67.opPattern","COPY",BODY,{"derivedFrom":makeQuery(id+"F66.opPattern","COPY",BODY,{"derivedFrom":makeQuery(id+"F65.opPattern","COPY",BODY,{"derivedFrom":makeQuery(id+"F64.opPattern","COPY",BODY,{"derivedFrom":makeQuery(id+"F63.opPattern","COPY",BODY,{"derivedFrom":makeQuery(id+"F62.opPattern","COPY",BODY,{"derivedFrom":makeQuery(id+"F61.opPattern","COPY",BODY,{"derivedFrom":makeQuery(id+"F60.opPattern","COPY",BODY,{"derivedFrom":makeQuery(id+"F59.opPattern","COPY",BODY,{"derivedFrom":makeQuery(id+"F58.opPattern","COPY",BODY,{"derivedFrom":makeQuery(id+"F56.opExtrude","SWEPT_BODY",BODY,{"disambiguationData":[OSD([sQuery(id+"F55.wireOp",EDGE,"E31.bottom"),sQuery(id+"F55.wireOp",EDGE,"E31.top"),sQuery(id+"F55.wireOp",EDGE,"E31.left"),sQuery(id+"F55.wireOp",EDGE,"E31.right")])]}),"instanceName":"1"}),"instanceName":"1"}),"instanceName":"1"}),"instanceName":"1"}),"instanceName":"1"}),"instanceName":"1"}),"instanceName":"1"}),"instanceName":"1"}),"instanceName":"1"}),"instanceName":"1"}),"instanceName":"1"}),"instanceName":"1"}),"instanceName":"1"}),"instanceName":"1"}),"instanceName":"1"});
            var Q34;
            Q34=makeQuery(id+"F73.opPattern","COPY",BODY,{"derivedFrom":makeQuery(id+"F72.opPattern","COPY",BODY,{"derivedFrom":makeQuery(id+"F71.opPattern","COPY",BODY,{"derivedFrom":makeQuery(id+"F70.opPattern","COPY",BODY,{"derivedFrom":makeQuery(id+"F69.opPattern","COPY",BODY,{"derivedFrom":makeQuery(id+"F68.opPattern","COPY",BODY,{"derivedFrom":makeQuery(id+"F67.opPattern","COPY",BODY,{"derivedFrom":makeQuery(id+"F66.opPattern","COPY",BODY,{"derivedFrom":makeQuery(id+"F65.opPattern","COPY",BODY,{"derivedFrom":makeQuery(id+"F64.opPattern","COPY",BODY,{"derivedFrom":makeQuery(id+"F63.opPattern","COPY",BODY,{"derivedFrom":makeQuery(id+"F62.opPattern","COPY",BODY,{"derivedFrom":makeQuery(id+"F61.opPattern","COPY",BODY,{"derivedFrom":makeQuery(id+"F60.opPattern","COPY",BODY,{"derivedFrom":makeQuery(id+"F59.opPattern","COPY",BODY,{"derivedFrom":makeQuery(id+"F58.opPattern","COPY",BODY,{"derivedFrom":makeQuery(id+"F56.opExtrude","SWEPT_BODY",BODY,{"disambiguationData":[OSD([sQuery(id+"F55.wireOp",EDGE,"E31.bottom"),sQuery(id+"F55.wireOp",EDGE,"E31.top"),sQuery(id+"F55.wireOp",EDGE,"E31.left"),sQuery(id+"F55.wireOp",EDGE,"E31.right")])]}),"instanceName":"1"}),"instanceName":"1"}),"instanceName":"1"}),"instanceName":"1"}),"instanceName":"1"}),"instanceName":"1"}),"instanceName":"1"}),"instanceName":"1"}),"instanceName":"1"}),"instanceName":"1"}),"instanceName":"1"}),"instanceName":"1"}),"instanceName":"1"}),"instanceName":"1"}),"instanceName":"1"}),"instanceName":"1"});
            var Q35;
            Q35=makeQuery(id+"F74.opPattern","COPY",BODY,{"derivedFrom":makeQuery(id+"F73.opPattern","COPY",BODY,{"derivedFrom":makeQuery(id+"F72.opPattern","COPY",BODY,{"derivedFrom":makeQuery(id+"F71.opPattern","COPY",BODY,{"derivedFrom":makeQuery(id+"F70.opPattern","COPY",BODY,{"derivedFrom":makeQuery(id+"F69.opPattern","COPY",BODY,{"derivedFrom":makeQuery(id+"F68.opPattern","COPY",BODY,{"derivedFrom":makeQuery(id+"F67.opPattern","COPY",BODY,{"derivedFrom":makeQuery(id+"F66.opPattern","COPY",BODY,{"derivedFrom":makeQuery(id+"F65.opPattern","COPY",BODY,{"derivedFrom":makeQuery(id+"F64.opPattern","COPY",BODY,{"derivedFrom":makeQuery(id+"F63.opPattern","COPY",BODY,{"derivedFrom":makeQuery(id+"F62.opPattern","COPY",BODY,{"derivedFrom":makeQuery(id+"F61.opPattern","COPY",BODY,{"derivedFrom":makeQuery(id+"F60.opPattern","COPY",BODY,{"derivedFrom":makeQuery(id+"F59.opPattern","COPY",BODY,{"derivedFrom":makeQuery(id+"F58.opPattern","COPY",BODY,{"derivedFrom":makeQuery(id+"F56.opExtrude","SWEPT_BODY",BODY,{"disambiguationData":[OSD([sQuery(id+"F55.wireOp",EDGE,"E31.bottom"),sQuery(id+"F55.wireOp",EDGE,"E31.top"),sQuery(id+"F55.wireOp",EDGE,"E31.left"),sQuery(id+"F55.wireOp",EDGE,"E31.right")])]}),"instanceName":"1"}),"instanceName":"1"}),"instanceName":"1"}),"instanceName":"1"}),"instanceName":"1"}),"instanceName":"1"}),"instanceName":"1"}),"instanceName":"1"}),"instanceName":"1"}),"instanceName":"1"}),"instanceName":"1"}),"instanceName":"1"}),"instanceName":"1"}),"instanceName":"1"}),"instanceName":"1"}),"instanceName":"1"}),"instanceName":"1"});
            var Q36;
            Q36=makeQuery(id+"F75.opPattern","COPY",BODY,{"derivedFrom":makeQuery(id+"F74.opPattern","COPY",BODY,{"derivedFrom":makeQuery(id+"F73.opPattern","COPY",BODY,{"derivedFrom":makeQuery(id+"F72.opPattern","COPY",BODY,{"derivedFrom":makeQuery(id+"F71.opPattern","COPY",BODY,{"derivedFrom":makeQuery(id+"F70.opPattern","COPY",BODY,{"derivedFrom":makeQuery(id+"F69.opPattern","COPY",BODY,{"derivedFrom":makeQuery(id+"F68.opPattern","COPY",BODY,{"derivedFrom":makeQuery(id+"F67.opPattern","COPY",BODY,{"derivedFrom":makeQuery(id+"F66.opPattern","COPY",BODY,{"derivedFrom":makeQuery(id+"F65.opPattern","COPY",BODY,{"derivedFrom":makeQuery(id+"F64.opPattern","COPY",BODY,{"derivedFrom":makeQuery(id+"F63.opPattern","COPY",BODY,{"derivedFrom":makeQuery(id+"F62.opPattern","COPY",BODY,{"derivedFrom":makeQuery(id+"F61.opPattern","COPY",BODY,{"derivedFrom":makeQuery(id+"F60.opPattern","COPY",BODY,{"derivedFrom":makeQuery(id+"F59.opPattern","COPY",BODY,{"derivedFrom":makeQuery(id+"F58.opPattern","COPY",BODY,{"derivedFrom":makeQuery(id+"F56.opExtrude","SWEPT_BODY",BODY,{"disambiguationData":[OSD([sQuery(id+"F55.wireOp",EDGE,"E31.bottom"),sQuery(id+"F55.wireOp",EDGE,"E31.top"),sQuery(id+"F55.wireOp",EDGE,"E31.left"),sQuery(id+"F55.wireOp",EDGE,"E31.right")])]}),"instanceName":"1"}),"instanceName":"1"}),"instanceName":"1"}),"instanceName":"1"}),"instanceName":"1"}),"instanceName":"1"}),"instanceName":"1"}),"instanceName":"1"}),"instanceName":"1"}),"instanceName":"1"}),"instanceName":"1"}),"instanceName":"1"}),"instanceName":"1"}),"instanceName":"1"}),"instanceName":"1"}),"instanceName":"1"}),"instanceName":"1"}),"instanceName":"1"});
            var Q37;
            Q37=makeQuery(id+"F76.opPattern","COPY",BODY,{"derivedFrom":makeQuery(id+"F75.opPattern","COPY",BODY,{"derivedFrom":makeQuery(id+"F74.opPattern","COPY",BODY,{"derivedFrom":makeQuery(id+"F73.opPattern","COPY",BODY,{"derivedFrom":makeQuery(id+"F72.opPattern","COPY",BODY,{"derivedFrom":makeQuery(id+"F71.opPattern","COPY",BODY,{"derivedFrom":makeQuery(id+"F70.opPattern","COPY",BODY,{"derivedFrom":makeQuery(id+"F69.opPattern","COPY",BODY,{"derivedFrom":makeQuery(id+"F68.opPattern","COPY",BODY,{"derivedFrom":makeQuery(id+"F67.opPattern","COPY",BODY,{"derivedFrom":makeQuery(id+"F66.opPattern","COPY",BODY,{"derivedFrom":makeQuery(id+"F65.opPattern","COPY",BODY,{"derivedFrom":makeQuery(id+"F64.opPattern","COPY",BODY,{"derivedFrom":makeQuery(id+"F63.opPattern","COPY",BODY,{"derivedFrom":makeQuery(id+"F62.opPattern","COPY",BODY,{"derivedFrom":makeQuery(id+"F61.opPattern","COPY",BODY,{"derivedFrom":makeQuery(id+"F60.opPattern","COPY",BODY,{"derivedFrom":makeQuery(id+"F59.opPattern","COPY",BODY,{"derivedFrom":makeQuery(id+"F58.opPattern","COPY",BODY,{"derivedFrom":makeQuery(id+"F56.opExtrude","SWEPT_BODY",BODY,{"disambiguationData":[OSD([sQuery(id+"F55.wireOp",EDGE,"E31.bottom"),sQuery(id+"F55.wireOp",EDGE,"E31.top"),sQuery(id+"F55.wireOp",EDGE,"E31.left"),sQuery(id+"F55.wireOp",EDGE,"E31.right")])]}),"instanceName":"1"}),"instanceName":"1"}),"instanceName":"1"}),"instanceName":"1"}),"instanceName":"1"}),"instanceName":"1"}),"instanceName":"1"}),"instanceName":"1"}),"instanceName":"1"}),"instanceName":"1"}),"instanceName":"1"}),"instanceName":"1"}),"instanceName":"1"}),"instanceName":"1"}),"instanceName":"1"}),"instanceName":"1"}),"instanceName":"1"}),"instanceName":"1"}),"instanceName":"1"});
            var Q38;
            Q38=makeQuery(id+"F77.opPattern","COPY",BODY,{"derivedFrom":makeQuery(id+"F76.opPattern","COPY",BODY,{"derivedFrom":makeQuery(id+"F75.opPattern","COPY",BODY,{"derivedFrom":makeQuery(id+"F74.opPattern","COPY",BODY,{"derivedFrom":makeQuery(id+"F73.opPattern","COPY",BODY,{"derivedFrom":makeQuery(id+"F72.opPattern","COPY",BODY,{"derivedFrom":makeQuery(id+"F71.opPattern","COPY",BODY,{"derivedFrom":makeQuery(id+"F70.opPattern","COPY",BODY,{"derivedFrom":makeQuery(id+"F69.opPattern","COPY",BODY,{"derivedFrom":makeQuery(id+"F68.opPattern","COPY",BODY,{"derivedFrom":makeQuery(id+"F67.opPattern","COPY",BODY,{"derivedFrom":makeQuery(id+"F66.opPattern","COPY",BODY,{"derivedFrom":makeQuery(id+"F65.opPattern","COPY",BODY,{"derivedFrom":makeQuery(id+"F64.opPattern","COPY",BODY,{"derivedFrom":makeQuery(id+"F63.opPattern","COPY",BODY,{"derivedFrom":makeQuery(id+"F62.opPattern","COPY",BODY,{"derivedFrom":makeQuery(id+"F61.opPattern","COPY",BODY,{"derivedFrom":makeQuery(id+"F60.opPattern","COPY",BODY,{"derivedFrom":makeQuery(id+"F59.opPattern","COPY",BODY,{"derivedFrom":makeQuery(id+"F58.opPattern","COPY",BODY,{"derivedFrom":makeQuery(id+"F56.opExtrude","SWEPT_BODY",BODY,{"disambiguationData":[OSD([sQuery(id+"F55.wireOp",EDGE,"E31.bottom"),sQuery(id+"F55.wireOp",EDGE,"E31.top"),sQuery(id+"F55.wireOp",EDGE,"E31.left"),sQuery(id+"F55.wireOp",EDGE,"E31.right")])]}),"instanceName":"1"}),"instanceName":"1"}),"instanceName":"1"}),"instanceName":"1"}),"instanceName":"1"}),"instanceName":"1"}),"instanceName":"1"}),"instanceName":"1"}),"instanceName":"1"}),"instanceName":"1"}),"instanceName":"1"}),"instanceName":"1"}),"instanceName":"1"}),"instanceName":"1"}),"instanceName":"1"}),"instanceName":"1"}),"instanceName":"1"}),"instanceName":"1"}),"instanceName":"1"}),"instanceName":"1"});
            var Q39;
            Q39=makeQuery(id+"F78.opPattern","COPY",BODY,{"derivedFrom":makeQuery(id+"F77.opPattern","COPY",BODY,{"derivedFrom":makeQuery(id+"F76.opPattern","COPY",BODY,{"derivedFrom":makeQuery(id+"F75.opPattern","COPY",BODY,{"derivedFrom":makeQuery(id+"F74.opPattern","COPY",BODY,{"derivedFrom":makeQuery(id+"F73.opPattern","COPY",BODY,{"derivedFrom":makeQuery(id+"F72.opPattern","COPY",BODY,{"derivedFrom":makeQuery(id+"F71.opPattern","COPY",BODY,{"derivedFrom":makeQuery(id+"F70.opPattern","COPY",BODY,{"derivedFrom":makeQuery(id+"F69.opPattern","COPY",BODY,{"derivedFrom":makeQuery(id+"F68.opPattern","COPY",BODY,{"derivedFrom":makeQuery(id+"F67.opPattern","COPY",BODY,{"derivedFrom":makeQuery(id+"F66.opPattern","COPY",BODY,{"derivedFrom":makeQuery(id+"F65.opPattern","COPY",BODY,{"derivedFrom":makeQuery(id+"F64.opPattern","COPY",BODY,{"derivedFrom":makeQuery(id+"F63.opPattern","COPY",BODY,{"derivedFrom":makeQuery(id+"F62.opPattern","COPY",BODY,{"derivedFrom":makeQuery(id+"F61.opPattern","COPY",BODY,{"derivedFrom":makeQuery(id+"F60.opPattern","COPY",BODY,{"derivedFrom":makeQuery(id+"F59.opPattern","COPY",BODY,{"derivedFrom":makeQuery(id+"F58.opPattern","COPY",BODY,{"derivedFrom":makeQuery(id+"F56.opExtrude","SWEPT_BODY",BODY,{"disambiguationData":[OSD([sQuery(id+"F55.wireOp",EDGE,"E31.bottom"),sQuery(id+"F55.wireOp",EDGE,"E31.top"),sQuery(id+"F55.wireOp",EDGE,"E31.left"),sQuery(id+"F55.wireOp",EDGE,"E31.right")])]}),"instanceName":"1"}),"instanceName":"1"}),"instanceName":"1"}),"instanceName":"1"}),"instanceName":"1"}),"instanceName":"1"}),"instanceName":"1"}),"instanceName":"1"}),"instanceName":"1"}),"instanceName":"1"}),"instanceName":"1"}),"instanceName":"1"}),"instanceName":"1"}),"instanceName":"1"}),"instanceName":"1"}),"instanceName":"1"}),"instanceName":"1"}),"instanceName":"1"}),"instanceName":"1"}),"instanceName":"1"}),"instanceName":"1"});
            booleanBodies(context, id + "F88", {"operationType" : BooleanOperationType.SUBTRACTION, "tools" : qUnion([Q0]), "targets" : qUnion([Q1, Q2, Q3, Q4, Q5, Q6, Q7, Q8, Q9, Q10, Q11, Q12, Q13, Q14, Q15, Q16, Q17, Q18, Q19, Q20, Q21, Q22, Q23, Q24, Q25, Q26, Q27, Q28, Q29, Q30, Q31, Q32, Q33, Q34, Q35, Q36, Q37, Q38, Q39])});
        }
        {
            var Q0;
            Q0=qCreatedBy(makeId("Top.planeOp"),FACE);
            var sketch = newSketch(context, id + "F89", { "sketchPlane" : qUnion([Q0])});
            skLineSegment(sketch, "E32.bottom", {"start": v(0, 0) * mm, "end": v(740, 0) * mm});
            skLineSegment(sketch, "E32.top", {"start": v(0, -261.35) * mm, "end": v(740, -261.35) * mm});
            skLineSegment(sketch, "E32.left", {"start": v(0, 0) * mm, "end": v(0, -261.35) * mm});
            skLineSegment(sketch, "E32.right", {"start": v(740, 0) * mm, "end": v(740, -261.35) * mm});
            skSolve(sketch);
        }
        {
            var Q0;
            Q0 = qSketchRegion(id + "F89", true);
            extrude(context, id + "F90", {"entities" : qUnion([Q0]), "depth" : 285 * mm});
        }
        {
            var Q0;
            Q0=makeQuery(id+"F90.opExtrude","SWEPT_BODY",BODY,{"disambiguationData":[OSD([sQuery(id+"F89.wireOp",EDGE,"E32.bottom"),sQuery(id+"F89.wireOp",EDGE,"E32.top"),sQuery(id+"F89.wireOp",EDGE,"E32.left"),sQuery(id+"F89.wireOp",EDGE,"E32.right")])]});
            transform(context, id + "F91", {"entities" : qUnion([Q0]), "transformType" : TransformType.TRANSLATION_3D, "dx" : -764.7 * mm, "dy" : 100 * mm, "dz" : 2000 * mm, "makeCopy" : false});
        }
        {
            var Q0;
            Q0=makeQuery(id+"F90.opExtrude","SWEPT_BODY",BODY,{"disambiguationData":[OSD([sQuery(id+"F89.wireOp",EDGE,"E32.bottom"),sQuery(id+"F89.wireOp",EDGE,"E32.top"),sQuery(id+"F89.wireOp",EDGE,"E32.left"),sQuery(id+"F89.wireOp",EDGE,"E32.right")])]});
            var Q1;
            Q1=makeQuery(id+"F79.opPattern","COPY",BODY,{"derivedFrom":makeQuery(id+"F56.opExtrude","SWEPT_BODY",BODY,{"disambiguationData":[OSD([sQuery(id+"F55.wireOp",EDGE,"E31.bottom"),sQuery(id+"F55.wireOp",EDGE,"E31.top"),sQuery(id+"F55.wireOp",EDGE,"E31.left"),sQuery(id+"F55.wireOp",EDGE,"E31.right")])]}),"instanceName":"1"});
            var Q2;
            Q2=makeQuery(id+"F80.opPattern","COPY",BODY,{"derivedFrom":makeQuery(id+"F79.opPattern","COPY",BODY,{"derivedFrom":makeQuery(id+"F56.opExtrude","SWEPT_BODY",BODY,{"disambiguationData":[OSD([sQuery(id+"F55.wireOp",EDGE,"E31.bottom"),sQuery(id+"F55.wireOp",EDGE,"E31.top"),sQuery(id+"F55.wireOp",EDGE,"E31.left"),sQuery(id+"F55.wireOp",EDGE,"E31.right")])]}),"instanceName":"1"}),"instanceName":"1"});
            var Q3;
            Q3=makeQuery(id+"F81.opPattern","COPY",BODY,{"derivedFrom":makeQuery(id+"F80.opPattern","COPY",BODY,{"derivedFrom":makeQuery(id+"F79.opPattern","COPY",BODY,{"derivedFrom":makeQuery(id+"F56.opExtrude","SWEPT_BODY",BODY,{"disambiguationData":[OSD([sQuery(id+"F55.wireOp",EDGE,"E31.bottom"),sQuery(id+"F55.wireOp",EDGE,"E31.top"),sQuery(id+"F55.wireOp",EDGE,"E31.left"),sQuery(id+"F55.wireOp",EDGE,"E31.right")])]}),"instanceName":"1"}),"instanceName":"1"}),"instanceName":"1"});
            var Q4;
            Q4=makeQuery(id+"F82.opPattern","COPY",BODY,{"derivedFrom":makeQuery(id+"F81.opPattern","COPY",BODY,{"derivedFrom":makeQuery(id+"F80.opPattern","COPY",BODY,{"derivedFrom":makeQuery(id+"F79.opPattern","COPY",BODY,{"derivedFrom":makeQuery(id+"F56.opExtrude","SWEPT_BODY",BODY,{"disambiguationData":[OSD([sQuery(id+"F55.wireOp",EDGE,"E31.bottom"),sQuery(id+"F55.wireOp",EDGE,"E31.top"),sQuery(id+"F55.wireOp",EDGE,"E31.left"),sQuery(id+"F55.wireOp",EDGE,"E31.right")])]}),"instanceName":"1"}),"instanceName":"1"}),"instanceName":"1"}),"instanceName":"1"});
            var Q5;
            Q5=makeQuery(id+"F83.opPattern","COPY",BODY,{"derivedFrom":makeQuery(id+"F82.opPattern","COPY",BODY,{"derivedFrom":makeQuery(id+"F81.opPattern","COPY",BODY,{"derivedFrom":makeQuery(id+"F80.opPattern","COPY",BODY,{"derivedFrom":makeQuery(id+"F79.opPattern","COPY",BODY,{"derivedFrom":makeQuery(id+"F56.opExtrude","SWEPT_BODY",BODY,{"disambiguationData":[OSD([sQuery(id+"F55.wireOp",EDGE,"E31.bottom"),sQuery(id+"F55.wireOp",EDGE,"E31.top"),sQuery(id+"F55.wireOp",EDGE,"E31.left"),sQuery(id+"F55.wireOp",EDGE,"E31.right")])]}),"instanceName":"1"}),"instanceName":"1"}),"instanceName":"1"}),"instanceName":"1"}),"instanceName":"1"});
            var Q6;
            Q6=makeQuery(id+"F84.opPattern","COPY",BODY,{"derivedFrom":makeQuery(id+"F83.opPattern","COPY",BODY,{"derivedFrom":makeQuery(id+"F82.opPattern","COPY",BODY,{"derivedFrom":makeQuery(id+"F81.opPattern","COPY",BODY,{"derivedFrom":makeQuery(id+"F80.opPattern","COPY",BODY,{"derivedFrom":makeQuery(id+"F79.opPattern","COPY",BODY,{"derivedFrom":makeQuery(id+"F56.opExtrude","SWEPT_BODY",BODY,{"disambiguationData":[OSD([sQuery(id+"F55.wireOp",EDGE,"E31.bottom"),sQuery(id+"F55.wireOp",EDGE,"E31.top"),sQuery(id+"F55.wireOp",EDGE,"E31.left"),sQuery(id+"F55.wireOp",EDGE,"E31.right")])]}),"instanceName":"1"}),"instanceName":"1"}),"instanceName":"1"}),"instanceName":"1"}),"instanceName":"1"}),"instanceName":"1"});
            var Q7;
            Q7=makeQuery(id+"F85.opPattern","COPY",BODY,{"derivedFrom":makeQuery(id+"F84.opPattern","COPY",BODY,{"derivedFrom":makeQuery(id+"F83.opPattern","COPY",BODY,{"derivedFrom":makeQuery(id+"F82.opPattern","COPY",BODY,{"derivedFrom":makeQuery(id+"F81.opPattern","COPY",BODY,{"derivedFrom":makeQuery(id+"F80.opPattern","COPY",BODY,{"derivedFrom":makeQuery(id+"F79.opPattern","COPY",BODY,{"derivedFrom":makeQuery(id+"F56.opExtrude","SWEPT_BODY",BODY,{"disambiguationData":[OSD([sQuery(id+"F55.wireOp",EDGE,"E31.bottom"),sQuery(id+"F55.wireOp",EDGE,"E31.top"),sQuery(id+"F55.wireOp",EDGE,"E31.left"),sQuery(id+"F55.wireOp",EDGE,"E31.right")])]}),"instanceName":"1"}),"instanceName":"1"}),"instanceName":"1"}),"instanceName":"1"}),"instanceName":"1"}),"instanceName":"1"}),"instanceName":"1"});
            var Q8;
            Q8=makeQuery(id+"F86.opPattern","COPY",BODY,{"derivedFrom":makeQuery(id+"F79.opPattern","COPY",BODY,{"derivedFrom":makeQuery(id+"F56.opExtrude","SWEPT_BODY",BODY,{"disambiguationData":[OSD([sQuery(id+"F55.wireOp",EDGE,"E31.bottom"),sQuery(id+"F55.wireOp",EDGE,"E31.top"),sQuery(id+"F55.wireOp",EDGE,"E31.left"),sQuery(id+"F55.wireOp",EDGE,"E31.right")])]}),"instanceName":"1"}),"instanceName":"1"});
            var Q9;
            Q9=makeQuery(id+"F86.opPattern","COPY",BODY,{"derivedFrom":makeQuery(id+"F80.opPattern","COPY",BODY,{"derivedFrom":makeQuery(id+"F79.opPattern","COPY",BODY,{"derivedFrom":makeQuery(id+"F56.opExtrude","SWEPT_BODY",BODY,{"disambiguationData":[OSD([sQuery(id+"F55.wireOp",EDGE,"E31.bottom"),sQuery(id+"F55.wireOp",EDGE,"E31.top"),sQuery(id+"F55.wireOp",EDGE,"E31.left"),sQuery(id+"F55.wireOp",EDGE,"E31.right")])]}),"instanceName":"1"}),"instanceName":"1"}),"instanceName":"1"});
            booleanBodies(context, id + "F92", {"operationType" : BooleanOperationType.SUBTRACTION, "tools" : qUnion([Q0]), "targets" : qUnion([Q1, Q2, Q3, Q4, Q5, Q6, Q7, Q8, Q9])});
        }
        {
            var Q0;
            Q0=qCreatedBy(makeId("Top.planeOp"),FACE);
            var sketch = newSketch(context, id + "F93", { "sketchPlane" : qUnion([Q0])});
            skLineSegment(sketch, "E33.bottom", {"start": v(0, 0) * mm, "end": v(69.69, 0) * mm});
            skLineSegment(sketch, "E33.top", {"start": v(0, 34.32) * mm, "end": v(69.69, 34.32) * mm});
            skLineSegment(sketch, "E33.left", {"start": v(0, 0) * mm, "end": v(0, 34.32) * mm});
            skLineSegment(sketch, "E33.right", {"start": v(69.69, 0) * mm, "end": v(69.69, 34.32) * mm});
            skSolve(sketch);
        }
        {
            var Q0;
            Q0 = qSketchRegion(id + "F93", true);
            extrude(context, id + "F94", {"entities" : qUnion([Q0]), "depth" : 2285 * mm});
        }
        {
            var Q0;
            Q0=makeQuery(id+"F94.opExtrude","SWEPT_BODY",BODY,{"disambiguationData":[OSD([sQuery(id+"F93.wireOp",EDGE,"E33.bottom"),sQuery(id+"F93.wireOp",EDGE,"E33.top"),sQuery(id+"F93.wireOp",EDGE,"E33.left"),sQuery(id+"F93.wireOp",EDGE,"E33.right")])]});
            transform(context, id + "F95", {"entities" : qUnion([Q0]), "transformType" : TransformType.TRANSLATION_3D, "dx" : -24.7 * mm, "dy" : 0 * mm, "dz" : 0 * mm, "makeCopy" : false});
        }
        {
            var Q0;
            Q0=makeQuery(id+"F94.opExtrude","SWEPT_BODY",BODY,{"disambiguationData":[OSD([sQuery(id+"F93.wireOp",EDGE,"E33.bottom"),sQuery(id+"F93.wireOp",EDGE,"E33.top"),sQuery(id+"F93.wireOp",EDGE,"E33.left"),sQuery(id+"F93.wireOp",EDGE,"E33.right")])]});
            var Q1;
            Q1=makeQuery(id+"F86.opPattern","COPY",BODY,{"derivedFrom":makeQuery(id+"F80.opPattern","COPY",BODY,{"derivedFrom":makeQuery(id+"F79.opPattern","COPY",BODY,{"derivedFrom":makeQuery(id+"F56.opExtrude","SWEPT_BODY",BODY,{"disambiguationData":[OSD([sQuery(id+"F55.wireOp",EDGE,"E31.bottom"),sQuery(id+"F55.wireOp",EDGE,"E31.top"),sQuery(id+"F55.wireOp",EDGE,"E31.left"),sQuery(id+"F55.wireOp",EDGE,"E31.right")])]}),"instanceName":"1"}),"instanceName":"1"}),"instanceName":"1"});
            var Q2;
            Q2=makeQuery(id+"F56.opExtrude","SWEPT_BODY",BODY,{"disambiguationData":[OSD([sQuery(id+"F55.wireOp",EDGE,"E31.bottom"),sQuery(id+"F55.wireOp",EDGE,"E31.top"),sQuery(id+"F55.wireOp",EDGE,"E31.left"),sQuery(id+"F55.wireOp",EDGE,"E31.right")])]});
            var Q3;
            Q3=makeQuery(id+"F86.opPattern","COPY",BODY,{"derivedFrom":makeQuery(id+"F81.opPattern","COPY",BODY,{"derivedFrom":makeQuery(id+"F80.opPattern","COPY",BODY,{"derivedFrom":makeQuery(id+"F79.opPattern","COPY",BODY,{"derivedFrom":makeQuery(id+"F56.opExtrude","SWEPT_BODY",BODY,{"disambiguationData":[OSD([sQuery(id+"F55.wireOp",EDGE,"E31.bottom"),sQuery(id+"F55.wireOp",EDGE,"E31.top"),sQuery(id+"F55.wireOp",EDGE,"E31.left"),sQuery(id+"F55.wireOp",EDGE,"E31.right")])]}),"instanceName":"1"}),"instanceName":"1"}),"instanceName":"1"}),"instanceName":"1"});
            booleanBodies(context, id + "F96", {"operationType" : BooleanOperationType.SUBTRACTION, "tools" : qUnion([Q0]), "targets" : qUnion([Q1, Q2, Q3])});
        }
        {
            var Q0;
            Q0=makeQuery(id+"F58.opPattern","COPY",BODY,{"derivedFrom":makeQuery(id+"F56.opExtrude","SWEPT_BODY",BODY,{"disambiguationData":[OSD([sQuery(id+"F55.wireOp",EDGE,"E31.bottom"),sQuery(id+"F55.wireOp",EDGE,"E31.top"),sQuery(id+"F55.wireOp",EDGE,"E31.left"),sQuery(id+"F55.wireOp",EDGE,"E31.right")])]}),"instanceName":"1"});
            transform(context, id + "F97", {"entities" : qUnion([Q0]), "transformType" : TransformType.TRANSLATION_3D, "dx" : -960 * mm, "dy" : 0 * mm, "dz" : 0 * mm, "makeCopy" : true});
        }
        {
            var Q0;
            Q0=qCreatedBy(makeId("Top.planeOp"),FACE);
            var sketch = newSketch(context, id + "F98", { "sketchPlane" : qUnion([Q0])});
            skLineSegment(sketch, "E34.bottom", {"start": v(0, 0) * mm, "end": v(128.11, 0) * mm});
            skLineSegment(sketch, "E34.top", {"start": v(0, 21.37) * mm, "end": v(128.11, 21.37) * mm});
            skLineSegment(sketch, "E34.left", {"start": v(0, 0) * mm, "end": v(0, 21.37) * mm});
            skLineSegment(sketch, "E34.right", {"start": v(128.11, 0) * mm, "end": v(128.11, 21.37) * mm});
            skSolve(sketch);
        }
        {
            var Q0;
            Q0 = qSketchRegion(id + "F98", true);
            extrude(context, id + "F99", {"entities" : qUnion([Q0]), "depth" : 50 * mm});
        }
        {
            var Q0;
            Q0=makeQuery(id+"F99.opExtrude","SWEPT_BODY",BODY,{"disambiguationData":[OSD([sQuery(id+"F98.wireOp",EDGE,"E34.bottom"),sQuery(id+"F98.wireOp",EDGE,"E34.top"),sQuery(id+"F98.wireOp",EDGE,"E34.left"),sQuery(id+"F98.wireOp",EDGE,"E34.right")])]});
            transform(context, id + "F100", {"entities" : qUnion([Q0]), "transformType" : TransformType.TRANSLATION_3D, "dx" : -860 * mm, "dy" : 0 * mm, "dz" : 0 * mm, "makeCopy" : false});
        }
        {
            var Q0;
            Q0=makeQuery(id+"F99.opExtrude","SWEPT_BODY",BODY,{"disambiguationData":[OSD([sQuery(id+"F98.wireOp",EDGE,"E34.bottom"),sQuery(id+"F98.wireOp",EDGE,"E34.top"),sQuery(id+"F98.wireOp",EDGE,"E34.left"),sQuery(id+"F98.wireOp",EDGE,"E34.right")])]});
            var Q1;
            Q1=makeQuery(id+"F97.opPattern","COPY",BODY,{"derivedFrom":makeQuery(id+"F58.opPattern","COPY",BODY,{"derivedFrom":makeQuery(id+"F56.opExtrude","SWEPT_BODY",BODY,{"disambiguationData":[OSD([sQuery(id+"F55.wireOp",EDGE,"E31.bottom"),sQuery(id+"F55.wireOp",EDGE,"E31.top"),sQuery(id+"F55.wireOp",EDGE,"E31.left"),sQuery(id+"F55.wireOp",EDGE,"E31.right")])]}),"instanceName":"1"}),"instanceName":"1"});
            booleanBodies(context, id + "F101", {"operationType" : BooleanOperationType.SUBTRACTION, "tools" : qUnion([Q0]), "targets" : qUnion([Q1])});
        }
    });
